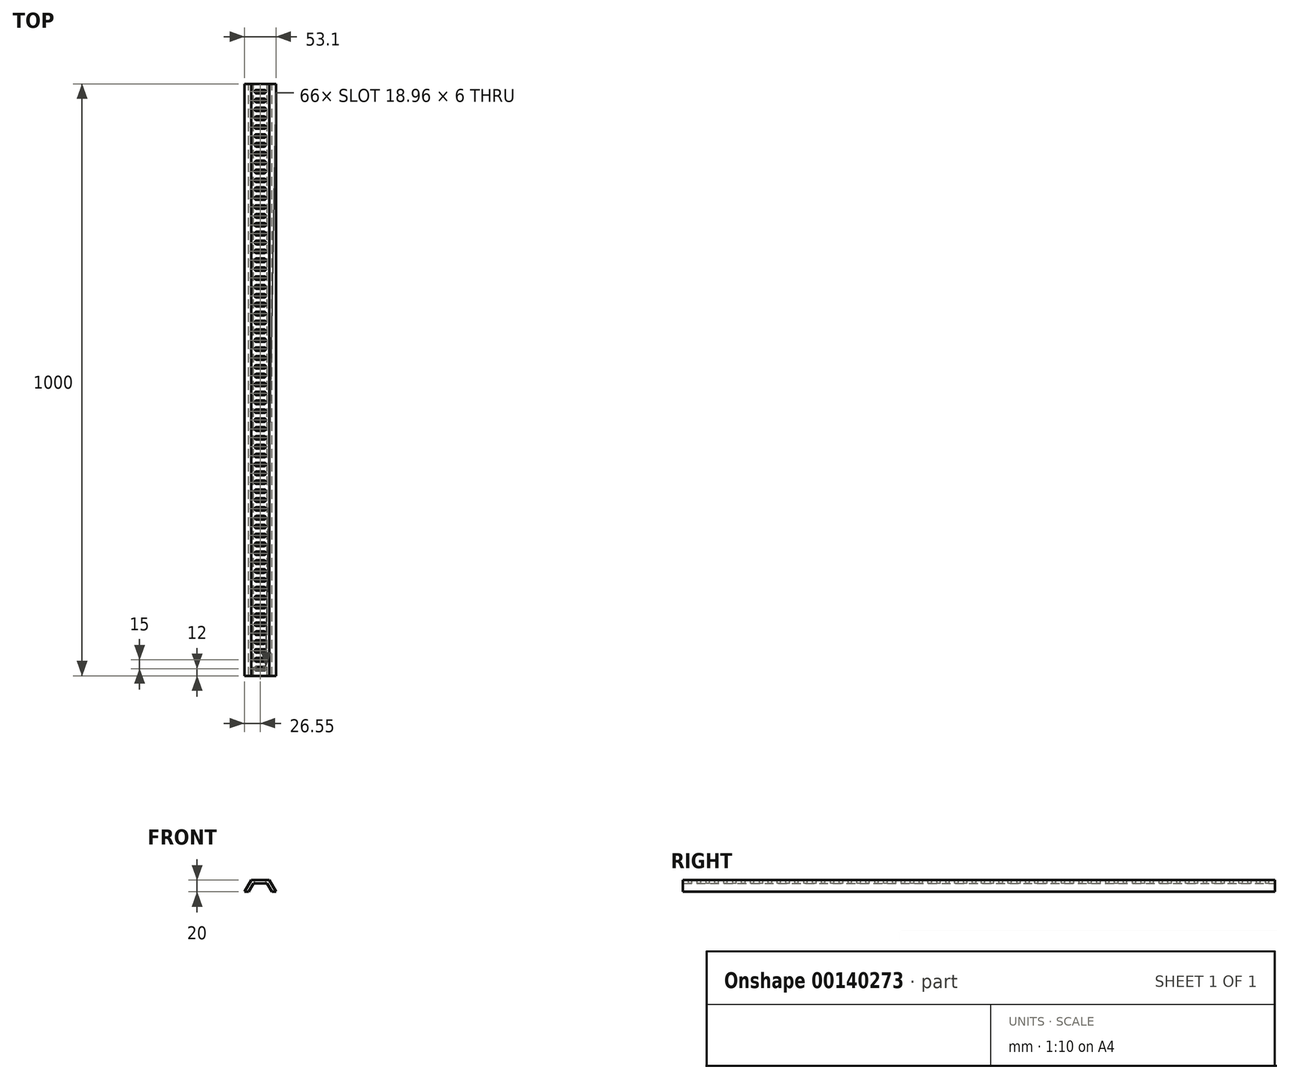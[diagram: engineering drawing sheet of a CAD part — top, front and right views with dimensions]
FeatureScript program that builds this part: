
annotation { "Feature Type Name" : "Feature", "Feature Type Description" : "" }
export const myFeature = defineFeature(function(context is Context, id is Id, definition is map)
    precondition{}
    {
        {
            var Q0;
            Q0=qCreatedBy(makeId("Front.planeOp"),FACE);
            var sketch = newSketch(context, id + "F0", { "sketchPlane" : qUnion([Q0])});
            skLineSegment(sketch, "E0", {"start": v(0, 20) * mm, "end": v(-49.9, 20) * mm, "construction": true});
            skLineSegment(sketch, "E1", {"start": v(0, 14) * mm, "end": v(-49.9, 14) * mm, "construction": true});
            skLineSegment(sketch, "E2", {"start": v(0, 20) * mm, "end": v(-15, 20) * mm});
            skLineSegment(sketch, "E3", {"start": v(-15, 20) * mm, "end": v(-26.55, 0) * mm});
            skLineSegment(sketch, "E4", {"start": v(-26.55, 0) * mm, "end": v(-19.5, 0) * mm});
            skLineSegment(sketch, "E5", {"start": v(-19.5, 0) * mm, "end": v(-11.41, 14) * mm});
            skLineSegment(sketch, "E6", {"start": v(-11.41, 14) * mm, "end": v(0, 14) * mm});
            skLineSegment(sketch, "E7.MirrorCS", {"start": v(0, 20) * mm, "end": v(15, 20) * mm});
            skLineSegment(sketch, "E8.MirrorCS", {"start": v(11.41, 14) * mm, "end": v(0, 14) * mm});
            skLineSegment(sketch, "E9.MirrorCS", {"start": v(19.5, 0) * mm, "end": v(11.41, 14) * mm});
            skLineSegment(sketch, "E10.MirrorCS", {"start": v(26.55, 0) * mm, "end": v(19.5, 0) * mm});
            skLineSegment(sketch, "E11.MirrorCS", {"start": v(15, 20) * mm, "end": v(26.55, 0) * mm});
            skLineSegment(sketch, "E12", {"start": v(-19.5, 0) * mm, "end": v(-24.78, 3.05) * mm, "construction": true});
            skSolve(sketch);
        }
        {
            var Q0;
            Q0=makeQuery(id+"F0.imprint","IMPRINT",FACE,{"disambiguationData":[TD([[makeQuery(id+"F0.imprint","IMPRINT",EDGE,{"derivedFrom":sQuery(id+"F0.wireOp",EDGE,"E2")}),1.0]])]});
            extrude(context, id + "F1", {"entities" : qUnion([Q0]), "depth" : 1000 * mm});
        }
        {
            var Q0;
            Q0=makeQuery(id+"F1.opExtrude","SWEPT_FACE",FACE,{"disambiguationData":[OSD([sQuery(id+"F0.wireOp",EDGE,"E2"),sQuery(id+"F0.wireOp",EDGE,"E7.MirrorCS")])]});
            var sketch = newSketch(context, id + "F2", { "sketchPlane" : qUnion([Q0])});
            skLineSegment(sketch, "E13.bottom", {"start": v(-6.48, -985) * mm, "end": v(6.48, -985) * mm});
            skLineSegment(sketch, "E13.top", {"start": v(-6.48, -991) * mm, "end": v(6.48, -991) * mm});
            skLineSegment(sketch, "E13.left", {"start": v(-9.48, -988) * mm, "end": v(-9.48, -988) * mm});
            skLineSegment(sketch, "E13.right", {"start": v(9.48, -988) * mm, "end": v(9.48, -988) * mm});
            skPoint(sketch, "E13.middle", {"position": v(0, -988) * mm});
            skPoint(sketch, "E14.visualSharp", {"position": v(-9.48, -985) * mm});
            skArc(sketch, "E14.filletArc", {"start": v(-6.48, -985) * mm, "mid": v(-8.6, -985.88) * mm, "end": v(-9.48, -988) * mm});
            skPoint(sketch, "E15.visualSharp", {"position": v(-9.48, -991) * mm});
            skArc(sketch, "E15.filletArc", {"start": v(-9.48, -988) * mm, "mid": v(-8.6, -990.12) * mm, "end": v(-6.48, -991) * mm});
            skPoint(sketch, "E16.visualSharp", {"position": v(9.48, -985) * mm});
            skArc(sketch, "E16.filletArc", {"start": v(9.48, -988) * mm, "mid": v(8.6, -985.88) * mm, "end": v(6.48, -985) * mm});
            skPoint(sketch, "E17.visualSharp", {"position": v(9.48, -991) * mm});
            skArc(sketch, "E17.filletArc", {"start": v(6.48, -991) * mm, "mid": v(8.6, -990.12) * mm, "end": v(9.48, -988) * mm});
            skLineSegment(sketch, "E18.0.1.0", {"start": v(-6.48, -976) * mm, "end": v(6.48, -976) * mm});
            skLineSegment(sketch, "E18.0.1.1", {"start": v(-6.48, -970) * mm, "end": v(6.48, -970) * mm});
            skPoint(sketch, "E18.0.1.2", {"position": v(9.48, -970) * mm});
            skPoint(sketch, "E18.0.1.3", {"position": v(-9.48, -976) * mm});
            skPoint(sketch, "E18.0.1.4", {"position": v(9.48, -976) * mm});
            skPoint(sketch, "E18.0.1.5", {"position": v(-9.48, -970) * mm});
            skPoint(sketch, "E18.0.1.6", {"position": v(0, -973) * mm});
            skArc(sketch, "E18.0.1.7", {"start": v(-9.48, -973) * mm, "mid": v(-8.6, -975.12) * mm, "end": v(-6.48, -976) * mm});
            skArc(sketch, "E18.0.1.8", {"start": v(-6.48, -970) * mm, "mid": v(-8.6, -970.88) * mm, "end": v(-9.48, -973) * mm});
            skArc(sketch, "E18.0.1.9", {"start": v(9.48, -973) * mm, "mid": v(8.6, -970.88) * mm, "end": v(6.48, -970) * mm});
            skArc(sketch, "E18.0.1.10", {"start": v(6.48, -976) * mm, "mid": v(8.6, -975.12) * mm, "end": v(9.48, -973) * mm});
            skLineSegment(sketch, "E18.0.2.0", {"start": v(-6.48, -961) * mm, "end": v(6.48, -961) * mm});
            skLineSegment(sketch, "E18.0.2.1", {"start": v(-6.48, -955) * mm, "end": v(6.48, -955) * mm});
            skPoint(sketch, "E18.0.2.2", {"position": v(9.48, -955) * mm});
            skPoint(sketch, "E18.0.2.3", {"position": v(-9.48, -961) * mm});
            skPoint(sketch, "E18.0.2.4", {"position": v(9.48, -961) * mm});
            skPoint(sketch, "E18.0.2.5", {"position": v(-9.48, -955) * mm});
            skPoint(sketch, "E18.0.2.6", {"position": v(0, -958) * mm});
            skArc(sketch, "E18.0.2.7", {"start": v(-9.48, -958) * mm, "mid": v(-8.6, -960.12) * mm, "end": v(-6.48, -961) * mm});
            skArc(sketch, "E18.0.2.8", {"start": v(-6.48, -955) * mm, "mid": v(-8.6, -955.88) * mm, "end": v(-9.48, -958) * mm});
            skArc(sketch, "E18.0.2.9", {"start": v(9.48, -958) * mm, "mid": v(8.6, -955.88) * mm, "end": v(6.48, -955) * mm});
            skArc(sketch, "E18.0.2.10", {"start": v(6.48, -961) * mm, "mid": v(8.6, -960.12) * mm, "end": v(9.48, -958) * mm});
            skLineSegment(sketch, "E18.0.3.0", {"start": v(-6.48, -946) * mm, "end": v(6.48, -946) * mm});
            skLineSegment(sketch, "E18.0.3.1", {"start": v(-6.48, -940) * mm, "end": v(6.48, -940) * mm});
            skPoint(sketch, "E18.0.3.2", {"position": v(9.48, -940) * mm});
            skPoint(sketch, "E18.0.3.3", {"position": v(-9.48, -946) * mm});
            skPoint(sketch, "E18.0.3.4", {"position": v(9.48, -946) * mm});
            skPoint(sketch, "E18.0.3.5", {"position": v(-9.48, -940) * mm});
            skPoint(sketch, "E18.0.3.6", {"position": v(0, -943) * mm});
            skArc(sketch, "E18.0.3.7", {"start": v(-9.48, -943) * mm, "mid": v(-8.6, -945.12) * mm, "end": v(-6.48, -946) * mm});
            skArc(sketch, "E18.0.3.8", {"start": v(-6.48, -940) * mm, "mid": v(-8.6, -940.88) * mm, "end": v(-9.48, -943) * mm});
            skArc(sketch, "E18.0.3.9", {"start": v(9.48, -943) * mm, "mid": v(8.6, -940.88) * mm, "end": v(6.48, -940) * mm});
            skArc(sketch, "E18.0.3.10", {"start": v(6.48, -946) * mm, "mid": v(8.6, -945.12) * mm, "end": v(9.48, -943) * mm});
            skLineSegment(sketch, "E18.0.4.0", {"start": v(-6.48, -931) * mm, "end": v(6.48, -931) * mm});
            skLineSegment(sketch, "E18.0.4.1", {"start": v(-6.48, -925) * mm, "end": v(6.48, -925) * mm});
            skPoint(sketch, "E18.0.4.2", {"position": v(9.48, -925) * mm});
            skPoint(sketch, "E18.0.4.3", {"position": v(-9.48, -931) * mm});
            skPoint(sketch, "E18.0.4.4", {"position": v(9.48, -931) * mm});
            skPoint(sketch, "E18.0.4.5", {"position": v(-9.48, -925) * mm});
            skPoint(sketch, "E18.0.4.6", {"position": v(0, -928) * mm});
            skArc(sketch, "E18.0.4.7", {"start": v(-9.48, -928) * mm, "mid": v(-8.6, -930.12) * mm, "end": v(-6.48, -931) * mm});
            skArc(sketch, "E18.0.4.8", {"start": v(-6.48, -925) * mm, "mid": v(-8.6, -925.88) * mm, "end": v(-9.48, -928) * mm});
            skArc(sketch, "E18.0.4.9", {"start": v(9.48, -928) * mm, "mid": v(8.6, -925.88) * mm, "end": v(6.48, -925) * mm});
            skArc(sketch, "E18.0.4.10", {"start": v(6.48, -931) * mm, "mid": v(8.6, -930.12) * mm, "end": v(9.48, -928) * mm});
            skLineSegment(sketch, "E18.0.5.0", {"start": v(-6.48, -916) * mm, "end": v(6.48, -916) * mm});
            skLineSegment(sketch, "E18.0.5.1", {"start": v(-6.48, -910) * mm, "end": v(6.48, -910) * mm});
            skPoint(sketch, "E18.0.5.2", {"position": v(9.48, -910) * mm});
            skPoint(sketch, "E18.0.5.3", {"position": v(-9.48, -916) * mm});
            skPoint(sketch, "E18.0.5.4", {"position": v(9.48, -916) * mm});
            skPoint(sketch, "E18.0.5.5", {"position": v(-9.48, -910) * mm});
            skPoint(sketch, "E18.0.5.6", {"position": v(0, -913) * mm});
            skArc(sketch, "E18.0.5.7", {"start": v(-9.48, -913) * mm, "mid": v(-8.6, -915.12) * mm, "end": v(-6.48, -916) * mm});
            skArc(sketch, "E18.0.5.8", {"start": v(-6.48, -910) * mm, "mid": v(-8.6, -910.88) * mm, "end": v(-9.48, -913) * mm});
            skArc(sketch, "E18.0.5.9", {"start": v(9.48, -913) * mm, "mid": v(8.6, -910.88) * mm, "end": v(6.48, -910) * mm});
            skArc(sketch, "E18.0.5.10", {"start": v(6.48, -916) * mm, "mid": v(8.6, -915.12) * mm, "end": v(9.48, -913) * mm});
            skLineSegment(sketch, "E18.0.6.0", {"start": v(-6.48, -901) * mm, "end": v(6.48, -901) * mm});
            skLineSegment(sketch, "E18.0.6.1", {"start": v(-6.48, -895) * mm, "end": v(6.48, -895) * mm});
            skPoint(sketch, "E18.0.6.2", {"position": v(9.48, -895) * mm});
            skPoint(sketch, "E18.0.6.3", {"position": v(-9.48, -901) * mm});
            skPoint(sketch, "E18.0.6.4", {"position": v(9.48, -901) * mm});
            skPoint(sketch, "E18.0.6.5", {"position": v(-9.48, -895) * mm});
            skPoint(sketch, "E18.0.6.6", {"position": v(0, -898) * mm});
            skArc(sketch, "E18.0.6.7", {"start": v(-9.48, -898) * mm, "mid": v(-8.6, -900.12) * mm, "end": v(-6.48, -901) * mm});
            skArc(sketch, "E18.0.6.8", {"start": v(-6.48, -895) * mm, "mid": v(-8.6, -895.88) * mm, "end": v(-9.48, -898) * mm});
            skArc(sketch, "E18.0.6.9", {"start": v(9.48, -898) * mm, "mid": v(8.6, -895.88) * mm, "end": v(6.48, -895) * mm});
            skArc(sketch, "E18.0.6.10", {"start": v(6.48, -901) * mm, "mid": v(8.6, -900.12) * mm, "end": v(9.48, -898) * mm});
            skLineSegment(sketch, "E18.0.7.0", {"start": v(-6.48, -886) * mm, "end": v(6.48, -886) * mm});
            skLineSegment(sketch, "E18.0.7.1", {"start": v(-6.48, -880) * mm, "end": v(6.48, -880) * mm});
            skPoint(sketch, "E18.0.7.2", {"position": v(9.48, -880) * mm});
            skPoint(sketch, "E18.0.7.3", {"position": v(-9.48, -886) * mm});
            skPoint(sketch, "E18.0.7.4", {"position": v(9.48, -886) * mm});
            skPoint(sketch, "E18.0.7.5", {"position": v(-9.48, -880) * mm});
            skPoint(sketch, "E18.0.7.6", {"position": v(0, -883) * mm});
            skArc(sketch, "E18.0.7.7", {"start": v(-9.48, -883) * mm, "mid": v(-8.6, -885.12) * mm, "end": v(-6.48, -886) * mm});
            skArc(sketch, "E18.0.7.8", {"start": v(-6.48, -880) * mm, "mid": v(-8.6, -880.88) * mm, "end": v(-9.48, -883) * mm});
            skArc(sketch, "E18.0.7.9", {"start": v(9.48, -883) * mm, "mid": v(8.6, -880.88) * mm, "end": v(6.48, -880) * mm});
            skArc(sketch, "E18.0.7.10", {"start": v(6.48, -886) * mm, "mid": v(8.6, -885.12) * mm, "end": v(9.48, -883) * mm});
            skLineSegment(sketch, "E18.0.8.0", {"start": v(-6.48, -871) * mm, "end": v(6.48, -871) * mm});
            skLineSegment(sketch, "E18.0.8.1", {"start": v(-6.48, -865) * mm, "end": v(6.48, -865) * mm});
            skPoint(sketch, "E18.0.8.2", {"position": v(9.48, -865) * mm});
            skPoint(sketch, "E18.0.8.3", {"position": v(-9.48, -871) * mm});
            skPoint(sketch, "E18.0.8.4", {"position": v(9.48, -871) * mm});
            skPoint(sketch, "E18.0.8.5", {"position": v(-9.48, -865) * mm});
            skPoint(sketch, "E18.0.8.6", {"position": v(0, -868) * mm});
            skArc(sketch, "E18.0.8.7", {"start": v(-9.48, -868) * mm, "mid": v(-8.6, -870.12) * mm, "end": v(-6.48, -871) * mm});
            skArc(sketch, "E18.0.8.8", {"start": v(-6.48, -865) * mm, "mid": v(-8.6, -865.88) * mm, "end": v(-9.48, -868) * mm});
            skArc(sketch, "E18.0.8.9", {"start": v(9.48, -868) * mm, "mid": v(8.6, -865.88) * mm, "end": v(6.48, -865) * mm});
            skArc(sketch, "E18.0.8.10", {"start": v(6.48, -871) * mm, "mid": v(8.6, -870.12) * mm, "end": v(9.48, -868) * mm});
            skLineSegment(sketch, "E18.0.9.0", {"start": v(-6.48, -856) * mm, "end": v(6.48, -856) * mm});
            skLineSegment(sketch, "E18.0.9.1", {"start": v(-6.48, -850) * mm, "end": v(6.48, -850) * mm});
            skPoint(sketch, "E18.0.9.2", {"position": v(9.48, -850) * mm});
            skPoint(sketch, "E18.0.9.3", {"position": v(-9.48, -856) * mm});
            skPoint(sketch, "E18.0.9.4", {"position": v(9.48, -856) * mm});
            skPoint(sketch, "E18.0.9.5", {"position": v(-9.48, -850) * mm});
            skPoint(sketch, "E18.0.9.6", {"position": v(0, -853) * mm});
            skArc(sketch, "E18.0.9.7", {"start": v(-9.48, -853) * mm, "mid": v(-8.6, -855.12) * mm, "end": v(-6.48, -856) * mm});
            skArc(sketch, "E18.0.9.8", {"start": v(-6.48, -850) * mm, "mid": v(-8.6, -850.88) * mm, "end": v(-9.48, -853) * mm});
            skArc(sketch, "E18.0.9.9", {"start": v(9.48, -853) * mm, "mid": v(8.6, -850.88) * mm, "end": v(6.48, -850) * mm});
            skArc(sketch, "E18.0.9.10", {"start": v(6.48, -856) * mm, "mid": v(8.6, -855.12) * mm, "end": v(9.48, -853) * mm});
            skLineSegment(sketch, "E18.0.10.0", {"start": v(-6.48, -841) * mm, "end": v(6.48, -841) * mm});
            skLineSegment(sketch, "E18.0.10.1", {"start": v(-6.48, -835) * mm, "end": v(6.48, -835) * mm});
            skPoint(sketch, "E18.0.10.2", {"position": v(9.48, -835) * mm});
            skPoint(sketch, "E18.0.10.3", {"position": v(-9.48, -841) * mm});
            skPoint(sketch, "E18.0.10.4", {"position": v(9.48, -841) * mm});
            skPoint(sketch, "E18.0.10.5", {"position": v(-9.48, -835) * mm});
            skPoint(sketch, "E18.0.10.6", {"position": v(0, -838) * mm});
            skArc(sketch, "E18.0.10.7", {"start": v(-9.48, -838) * mm, "mid": v(-8.6, -840.12) * mm, "end": v(-6.48, -841) * mm});
            skArc(sketch, "E18.0.10.8", {"start": v(-6.48, -835) * mm, "mid": v(-8.6, -835.88) * mm, "end": v(-9.48, -838) * mm});
            skArc(sketch, "E18.0.10.9", {"start": v(9.48, -838) * mm, "mid": v(8.6, -835.88) * mm, "end": v(6.48, -835) * mm});
            skArc(sketch, "E18.0.10.10", {"start": v(6.48, -841) * mm, "mid": v(8.6, -840.12) * mm, "end": v(9.48, -838) * mm});
            skLineSegment(sketch, "E18.0.11.0", {"start": v(-6.48, -826) * mm, "end": v(6.48, -826) * mm});
            skLineSegment(sketch, "E18.0.11.1", {"start": v(-6.48, -820) * mm, "end": v(6.48, -820) * mm});
            skPoint(sketch, "E18.0.11.2", {"position": v(9.48, -820) * mm});
            skPoint(sketch, "E18.0.11.3", {"position": v(-9.48, -826) * mm});
            skPoint(sketch, "E18.0.11.4", {"position": v(9.48, -826) * mm});
            skPoint(sketch, "E18.0.11.5", {"position": v(-9.48, -820) * mm});
            skPoint(sketch, "E18.0.11.6", {"position": v(0, -823) * mm});
            skArc(sketch, "E18.0.11.7", {"start": v(-9.48, -823) * mm, "mid": v(-8.6, -825.12) * mm, "end": v(-6.48, -826) * mm});
            skArc(sketch, "E18.0.11.8", {"start": v(-6.48, -820) * mm, "mid": v(-8.6, -820.88) * mm, "end": v(-9.48, -823) * mm});
            skArc(sketch, "E18.0.11.9", {"start": v(9.48, -823) * mm, "mid": v(8.6, -820.88) * mm, "end": v(6.48, -820) * mm});
            skArc(sketch, "E18.0.11.10", {"start": v(6.48, -826) * mm, "mid": v(8.6, -825.12) * mm, "end": v(9.48, -823) * mm});
            skLineSegment(sketch, "E18.0.12.0", {"start": v(-6.48, -811) * mm, "end": v(6.48, -811) * mm});
            skLineSegment(sketch, "E18.0.12.1", {"start": v(-6.48, -805) * mm, "end": v(6.48, -805) * mm});
            skPoint(sketch, "E18.0.12.2", {"position": v(9.48, -805) * mm});
            skPoint(sketch, "E18.0.12.3", {"position": v(-9.48, -811) * mm});
            skPoint(sketch, "E18.0.12.4", {"position": v(9.48, -811) * mm});
            skPoint(sketch, "E18.0.12.5", {"position": v(-9.48, -805) * mm});
            skPoint(sketch, "E18.0.12.6", {"position": v(0, -808) * mm});
            skArc(sketch, "E18.0.12.7", {"start": v(-9.48, -808) * mm, "mid": v(-8.6, -810.12) * mm, "end": v(-6.48, -811) * mm});
            skArc(sketch, "E18.0.12.8", {"start": v(-6.48, -805) * mm, "mid": v(-8.6, -805.88) * mm, "end": v(-9.48, -808) * mm});
            skArc(sketch, "E18.0.12.9", {"start": v(9.48, -808) * mm, "mid": v(8.6, -805.88) * mm, "end": v(6.48, -805) * mm});
            skArc(sketch, "E18.0.12.10", {"start": v(6.48, -811) * mm, "mid": v(8.6, -810.12) * mm, "end": v(9.48, -808) * mm});
            skLineSegment(sketch, "E18.0.13.0", {"start": v(-6.48, -796) * mm, "end": v(6.48, -796) * mm});
            skLineSegment(sketch, "E18.0.13.1", {"start": v(-6.48, -790) * mm, "end": v(6.48, -790) * mm});
            skPoint(sketch, "E18.0.13.2", {"position": v(9.48, -790) * mm});
            skPoint(sketch, "E18.0.13.3", {"position": v(-9.48, -796) * mm});
            skPoint(sketch, "E18.0.13.4", {"position": v(9.48, -796) * mm});
            skPoint(sketch, "E18.0.13.5", {"position": v(-9.48, -790) * mm});
            skPoint(sketch, "E18.0.13.6", {"position": v(0, -793) * mm});
            skArc(sketch, "E18.0.13.7", {"start": v(-9.48, -793) * mm, "mid": v(-8.6, -795.12) * mm, "end": v(-6.48, -796) * mm});
            skArc(sketch, "E18.0.13.8", {"start": v(-6.48, -790) * mm, "mid": v(-8.6, -790.88) * mm, "end": v(-9.48, -793) * mm});
            skArc(sketch, "E18.0.13.9", {"start": v(9.48, -793) * mm, "mid": v(8.6, -790.88) * mm, "end": v(6.48, -790) * mm});
            skArc(sketch, "E18.0.13.10", {"start": v(6.48, -796) * mm, "mid": v(8.6, -795.12) * mm, "end": v(9.48, -793) * mm});
            skLineSegment(sketch, "E18.0.14.0", {"start": v(-6.48, -781) * mm, "end": v(6.48, -781) * mm});
            skLineSegment(sketch, "E18.0.14.1", {"start": v(-6.48, -775) * mm, "end": v(6.48, -775) * mm});
            skPoint(sketch, "E18.0.14.2", {"position": v(9.48, -775) * mm});
            skPoint(sketch, "E18.0.14.3", {"position": v(-9.48, -781) * mm});
            skPoint(sketch, "E18.0.14.4", {"position": v(9.48, -781) * mm});
            skPoint(sketch, "E18.0.14.5", {"position": v(-9.48, -775) * mm});
            skPoint(sketch, "E18.0.14.6", {"position": v(0, -778) * mm});
            skArc(sketch, "E18.0.14.7", {"start": v(-9.48, -778) * mm, "mid": v(-8.6, -780.12) * mm, "end": v(-6.48, -781) * mm});
            skArc(sketch, "E18.0.14.8", {"start": v(-6.48, -775) * mm, "mid": v(-8.6, -775.88) * mm, "end": v(-9.48, -778) * mm});
            skArc(sketch, "E18.0.14.9", {"start": v(9.48, -778) * mm, "mid": v(8.6, -775.88) * mm, "end": v(6.48, -775) * mm});
            skArc(sketch, "E18.0.14.10", {"start": v(6.48, -781) * mm, "mid": v(8.6, -780.12) * mm, "end": v(9.48, -778) * mm});
            skLineSegment(sketch, "E18.direction1", {"start": v(-9.48, -991) * mm, "end": v(21.55, -991) * mm, "construction": true});
            skLineSegment(sketch, "E18.direction2", {"start": v(-9.48, -991) * mm, "end": v(-9.48, -976) * mm, "construction": true});
            skLineSegment(sketch, "E19.0.0.15", {"start": v(-6.48, -766) * mm, "end": v(6.48, -766) * mm});
            skLineSegment(sketch, "E19.3.0.15", {"start": v(-6.48, -760) * mm, "end": v(6.48, -760) * mm});
            skPoint(sketch, "E19.6.0.15", {"position": v(9.48, -760) * mm});
            skPoint(sketch, "E19.7.0.15", {"position": v(-9.48, -766) * mm});
            skPoint(sketch, "E19.8.0.15", {"position": v(9.48, -766) * mm});
            skPoint(sketch, "E19.9.0.15", {"position": v(-9.48, -760) * mm});
            skPoint(sketch, "E19.10.0.15", {"position": v(0, -763) * mm});
            skArc(sketch, "E19.11.0.15", {"start": v(-9.48, -763) * mm, "mid": v(-8.6, -765.12) * mm, "end": v(-6.48, -766) * mm});
            skArc(sketch, "E19.15.0.15", {"start": v(-6.48, -760) * mm, "mid": v(-8.6, -760.88) * mm, "end": v(-9.48, -763) * mm});
            skArc(sketch, "E19.19.0.15", {"start": v(9.48, -763) * mm, "mid": v(8.6, -760.88) * mm, "end": v(6.48, -760) * mm});
            skArc(sketch, "E19.23.0.15", {"start": v(6.48, -766) * mm, "mid": v(8.6, -765.12) * mm, "end": v(9.48, -763) * mm});
            skLineSegment(sketch, "E19.0.0.16", {"start": v(-6.48, -751) * mm, "end": v(6.48, -751) * mm});
            skLineSegment(sketch, "E19.3.0.16", {"start": v(-6.48, -745) * mm, "end": v(6.48, -745) * mm});
            skPoint(sketch, "E19.6.0.16", {"position": v(9.48, -745) * mm});
            skPoint(sketch, "E19.7.0.16", {"position": v(-9.48, -751) * mm});
            skPoint(sketch, "E19.8.0.16", {"position": v(9.48, -751) * mm});
            skPoint(sketch, "E19.9.0.16", {"position": v(-9.48, -745) * mm});
            skPoint(sketch, "E19.10.0.16", {"position": v(0, -748) * mm});
            skArc(sketch, "E19.11.0.16", {"start": v(-9.48, -748) * mm, "mid": v(-8.6, -750.12) * mm, "end": v(-6.48, -751) * mm});
            skArc(sketch, "E19.15.0.16", {"start": v(-6.48, -745) * mm, "mid": v(-8.6, -745.88) * mm, "end": v(-9.48, -748) * mm});
            skArc(sketch, "E19.19.0.16", {"start": v(9.48, -748) * mm, "mid": v(8.6, -745.88) * mm, "end": v(6.48, -745) * mm});
            skArc(sketch, "E19.23.0.16", {"start": v(6.48, -751) * mm, "mid": v(8.6, -750.12) * mm, "end": v(9.48, -748) * mm});
            skLineSegment(sketch, "E19.0.0.17", {"start": v(-6.48, -736) * mm, "end": v(6.48, -736) * mm});
            skLineSegment(sketch, "E19.3.0.17", {"start": v(-6.48, -730) * mm, "end": v(6.48, -730) * mm});
            skPoint(sketch, "E19.6.0.17", {"position": v(9.48, -730) * mm});
            skPoint(sketch, "E19.7.0.17", {"position": v(-9.48, -736) * mm});
            skPoint(sketch, "E19.8.0.17", {"position": v(9.48, -736) * mm});
            skPoint(sketch, "E19.9.0.17", {"position": v(-9.48, -730) * mm});
            skPoint(sketch, "E19.10.0.17", {"position": v(0, -733) * mm});
            skArc(sketch, "E19.11.0.17", {"start": v(-9.48, -733) * mm, "mid": v(-8.6, -735.12) * mm, "end": v(-6.48, -736) * mm});
            skArc(sketch, "E19.15.0.17", {"start": v(-6.48, -730) * mm, "mid": v(-8.6, -730.88) * mm, "end": v(-9.48, -733) * mm});
            skArc(sketch, "E19.19.0.17", {"start": v(9.48, -733) * mm, "mid": v(8.6, -730.88) * mm, "end": v(6.48, -730) * mm});
            skArc(sketch, "E19.23.0.17", {"start": v(6.48, -736) * mm, "mid": v(8.6, -735.12) * mm, "end": v(9.48, -733) * mm});
            skLineSegment(sketch, "E19.0.0.18", {"start": v(-6.48, -721) * mm, "end": v(6.48, -721) * mm});
            skLineSegment(sketch, "E19.3.0.18", {"start": v(-6.48, -715) * mm, "end": v(6.48, -715) * mm});
            skPoint(sketch, "E19.6.0.18", {"position": v(9.48, -715) * mm});
            skPoint(sketch, "E19.7.0.18", {"position": v(-9.48, -721) * mm});
            skPoint(sketch, "E19.8.0.18", {"position": v(9.48, -721) * mm});
            skPoint(sketch, "E19.9.0.18", {"position": v(-9.48, -715) * mm});
            skPoint(sketch, "E19.10.0.18", {"position": v(0, -718) * mm});
            skArc(sketch, "E19.11.0.18", {"start": v(-9.48, -718) * mm, "mid": v(-8.6, -720.12) * mm, "end": v(-6.48, -721) * mm});
            skArc(sketch, "E19.15.0.18", {"start": v(-6.48, -715) * mm, "mid": v(-8.6, -715.88) * mm, "end": v(-9.48, -718) * mm});
            skArc(sketch, "E19.19.0.18", {"start": v(9.48, -718) * mm, "mid": v(8.6, -715.88) * mm, "end": v(6.48, -715) * mm});
            skArc(sketch, "E19.23.0.18", {"start": v(6.48, -721) * mm, "mid": v(8.6, -720.12) * mm, "end": v(9.48, -718) * mm});
            skLineSegment(sketch, "E19.0.0.19", {"start": v(-6.48, -706) * mm, "end": v(6.48, -706) * mm});
            skLineSegment(sketch, "E19.3.0.19", {"start": v(-6.48, -700) * mm, "end": v(6.48, -700) * mm});
            skPoint(sketch, "E19.6.0.19", {"position": v(9.48, -700) * mm});
            skPoint(sketch, "E19.7.0.19", {"position": v(-9.48, -706) * mm});
            skPoint(sketch, "E19.8.0.19", {"position": v(9.48, -706) * mm});
            skPoint(sketch, "E19.9.0.19", {"position": v(-9.48, -700) * mm});
            skPoint(sketch, "E19.10.0.19", {"position": v(0, -703) * mm});
            skArc(sketch, "E19.11.0.19", {"start": v(-9.48, -703) * mm, "mid": v(-8.6, -705.12) * mm, "end": v(-6.48, -706) * mm});
            skArc(sketch, "E19.15.0.19", {"start": v(-6.48, -700) * mm, "mid": v(-8.6, -700.88) * mm, "end": v(-9.48, -703) * mm});
            skArc(sketch, "E19.19.0.19", {"start": v(9.48, -703) * mm, "mid": v(8.6, -700.88) * mm, "end": v(6.48, -700) * mm});
            skArc(sketch, "E19.23.0.19", {"start": v(6.48, -706) * mm, "mid": v(8.6, -705.12) * mm, "end": v(9.48, -703) * mm});
            skLineSegment(sketch, "E19.0.0.20", {"start": v(-6.48, -691) * mm, "end": v(6.48, -691) * mm});
            skLineSegment(sketch, "E19.3.0.20", {"start": v(-6.48, -685) * mm, "end": v(6.48, -685) * mm});
            skPoint(sketch, "E19.6.0.20", {"position": v(9.48, -685) * mm});
            skPoint(sketch, "E19.7.0.20", {"position": v(-9.48, -691) * mm});
            skPoint(sketch, "E19.8.0.20", {"position": v(9.48, -691) * mm});
            skPoint(sketch, "E19.9.0.20", {"position": v(-9.48, -685) * mm});
            skPoint(sketch, "E19.10.0.20", {"position": v(0, -688) * mm});
            skArc(sketch, "E19.11.0.20", {"start": v(-9.48, -688) * mm, "mid": v(-8.6, -690.12) * mm, "end": v(-6.48, -691) * mm});
            skArc(sketch, "E19.15.0.20", {"start": v(-6.48, -685) * mm, "mid": v(-8.6, -685.88) * mm, "end": v(-9.48, -688) * mm});
            skArc(sketch, "E19.19.0.20", {"start": v(9.48, -688) * mm, "mid": v(8.6, -685.88) * mm, "end": v(6.48, -685) * mm});
            skArc(sketch, "E19.23.0.20", {"start": v(6.48, -691) * mm, "mid": v(8.6, -690.12) * mm, "end": v(9.48, -688) * mm});
            skLineSegment(sketch, "E19.0.0.21", {"start": v(-6.48, -676) * mm, "end": v(6.48, -676) * mm});
            skLineSegment(sketch, "E19.3.0.21", {"start": v(-6.48, -670) * mm, "end": v(6.48, -670) * mm});
            skPoint(sketch, "E19.6.0.21", {"position": v(9.48, -670) * mm});
            skPoint(sketch, "E19.7.0.21", {"position": v(-9.48, -676) * mm});
            skPoint(sketch, "E19.8.0.21", {"position": v(9.48, -676) * mm});
            skPoint(sketch, "E19.9.0.21", {"position": v(-9.48, -670) * mm});
            skPoint(sketch, "E19.10.0.21", {"position": v(0, -673) * mm});
            skArc(sketch, "E19.11.0.21", {"start": v(-9.48, -673) * mm, "mid": v(-8.6, -675.12) * mm, "end": v(-6.48, -676) * mm});
            skArc(sketch, "E19.15.0.21", {"start": v(-6.48, -670) * mm, "mid": v(-8.6, -670.88) * mm, "end": v(-9.48, -673) * mm});
            skArc(sketch, "E19.19.0.21", {"start": v(9.48, -673) * mm, "mid": v(8.6, -670.88) * mm, "end": v(6.48, -670) * mm});
            skArc(sketch, "E19.23.0.21", {"start": v(6.48, -676) * mm, "mid": v(8.6, -675.12) * mm, "end": v(9.48, -673) * mm});
            skLineSegment(sketch, "E19.0.0.22", {"start": v(-6.48, -661) * mm, "end": v(6.48, -661) * mm});
            skLineSegment(sketch, "E19.3.0.22", {"start": v(-6.48, -655) * mm, "end": v(6.48, -655) * mm});
            skPoint(sketch, "E19.6.0.22", {"position": v(9.48, -655) * mm});
            skPoint(sketch, "E19.7.0.22", {"position": v(-9.48, -661) * mm});
            skPoint(sketch, "E19.8.0.22", {"position": v(9.48, -661) * mm});
            skPoint(sketch, "E19.9.0.22", {"position": v(-9.48, -655) * mm});
            skPoint(sketch, "E19.10.0.22", {"position": v(0, -658) * mm});
            skArc(sketch, "E19.11.0.22", {"start": v(-9.48, -658) * mm, "mid": v(-8.6, -660.12) * mm, "end": v(-6.48, -661) * mm});
            skArc(sketch, "E19.15.0.22", {"start": v(-6.48, -655) * mm, "mid": v(-8.6, -655.88) * mm, "end": v(-9.48, -658) * mm});
            skArc(sketch, "E19.19.0.22", {"start": v(9.48, -658) * mm, "mid": v(8.6, -655.88) * mm, "end": v(6.48, -655) * mm});
            skArc(sketch, "E19.23.0.22", {"start": v(6.48, -661) * mm, "mid": v(8.6, -660.12) * mm, "end": v(9.48, -658) * mm});
            skLineSegment(sketch, "E19.0.0.23", {"start": v(-6.48, -646) * mm, "end": v(6.48, -646) * mm});
            skLineSegment(sketch, "E19.3.0.23", {"start": v(-6.48, -640) * mm, "end": v(6.48, -640) * mm});
            skPoint(sketch, "E19.6.0.23", {"position": v(9.48, -640) * mm});
            skPoint(sketch, "E19.7.0.23", {"position": v(-9.48, -646) * mm});
            skPoint(sketch, "E19.8.0.23", {"position": v(9.48, -646) * mm});
            skPoint(sketch, "E19.9.0.23", {"position": v(-9.48, -640) * mm});
            skPoint(sketch, "E19.10.0.23", {"position": v(0, -643) * mm});
            skArc(sketch, "E19.11.0.23", {"start": v(-9.48, -643) * mm, "mid": v(-8.6, -645.12) * mm, "end": v(-6.48, -646) * mm});
            skArc(sketch, "E19.15.0.23", {"start": v(-6.48, -640) * mm, "mid": v(-8.6, -640.88) * mm, "end": v(-9.48, -643) * mm});
            skArc(sketch, "E19.19.0.23", {"start": v(9.48, -643) * mm, "mid": v(8.6, -640.88) * mm, "end": v(6.48, -640) * mm});
            skArc(sketch, "E19.23.0.23", {"start": v(6.48, -646) * mm, "mid": v(8.6, -645.12) * mm, "end": v(9.48, -643) * mm});
            skLineSegment(sketch, "E19.0.0.24", {"start": v(-6.48, -631) * mm, "end": v(6.48, -631) * mm});
            skLineSegment(sketch, "E19.3.0.24", {"start": v(-6.48, -625) * mm, "end": v(6.48, -625) * mm});
            skPoint(sketch, "E19.6.0.24", {"position": v(9.48, -625) * mm});
            skPoint(sketch, "E19.7.0.24", {"position": v(-9.48, -631) * mm});
            skPoint(sketch, "E19.8.0.24", {"position": v(9.48, -631) * mm});
            skPoint(sketch, "E19.9.0.24", {"position": v(-9.48, -625) * mm});
            skPoint(sketch, "E19.10.0.24", {"position": v(0, -628) * mm});
            skArc(sketch, "E19.11.0.24", {"start": v(-9.48, -628) * mm, "mid": v(-8.6, -630.12) * mm, "end": v(-6.48, -631) * mm});
            skArc(sketch, "E19.15.0.24", {"start": v(-6.48, -625) * mm, "mid": v(-8.6, -625.88) * mm, "end": v(-9.48, -628) * mm});
            skArc(sketch, "E19.19.0.24", {"start": v(9.48, -628) * mm, "mid": v(8.6, -625.88) * mm, "end": v(6.48, -625) * mm});
            skArc(sketch, "E19.23.0.24", {"start": v(6.48, -631) * mm, "mid": v(8.6, -630.12) * mm, "end": v(9.48, -628) * mm});
            skLineSegment(sketch, "E19.0.0.25", {"start": v(-6.48, -616) * mm, "end": v(6.48, -616) * mm});
            skLineSegment(sketch, "E19.3.0.25", {"start": v(-6.48, -610) * mm, "end": v(6.48, -610) * mm});
            skPoint(sketch, "E19.6.0.25", {"position": v(9.48, -610) * mm});
            skPoint(sketch, "E19.7.0.25", {"position": v(-9.48, -616) * mm});
            skPoint(sketch, "E19.8.0.25", {"position": v(9.48, -616) * mm});
            skPoint(sketch, "E19.9.0.25", {"position": v(-9.48, -610) * mm});
            skPoint(sketch, "E19.10.0.25", {"position": v(0, -613) * mm});
            skArc(sketch, "E19.11.0.25", {"start": v(-9.48, -613) * mm, "mid": v(-8.6, -615.12) * mm, "end": v(-6.48, -616) * mm});
            skArc(sketch, "E19.15.0.25", {"start": v(-6.48, -610) * mm, "mid": v(-8.6, -610.88) * mm, "end": v(-9.48, -613) * mm});
            skArc(sketch, "E19.19.0.25", {"start": v(9.48, -613) * mm, "mid": v(8.6, -610.88) * mm, "end": v(6.48, -610) * mm});
            skArc(sketch, "E19.23.0.25", {"start": v(6.48, -616) * mm, "mid": v(8.6, -615.12) * mm, "end": v(9.48, -613) * mm});
            skLineSegment(sketch, "E19.0.0.26", {"start": v(-6.48, -601) * mm, "end": v(6.48, -601) * mm});
            skLineSegment(sketch, "E19.3.0.26", {"start": v(-6.48, -595) * mm, "end": v(6.48, -595) * mm});
            skPoint(sketch, "E19.6.0.26", {"position": v(9.48, -595) * mm});
            skPoint(sketch, "E19.7.0.26", {"position": v(-9.48, -601) * mm});
            skPoint(sketch, "E19.8.0.26", {"position": v(9.48, -601) * mm});
            skPoint(sketch, "E19.9.0.26", {"position": v(-9.48, -595) * mm});
            skPoint(sketch, "E19.10.0.26", {"position": v(0, -598) * mm});
            skArc(sketch, "E19.11.0.26", {"start": v(-9.48, -598) * mm, "mid": v(-8.6, -600.12) * mm, "end": v(-6.48, -601) * mm});
            skArc(sketch, "E19.15.0.26", {"start": v(-6.48, -595) * mm, "mid": v(-8.6, -595.88) * mm, "end": v(-9.48, -598) * mm});
            skArc(sketch, "E19.19.0.26", {"start": v(9.48, -598) * mm, "mid": v(8.6, -595.88) * mm, "end": v(6.48, -595) * mm});
            skArc(sketch, "E19.23.0.26", {"start": v(6.48, -601) * mm, "mid": v(8.6, -600.12) * mm, "end": v(9.48, -598) * mm});
            skLineSegment(sketch, "E19.0.0.27", {"start": v(-6.48, -586) * mm, "end": v(6.48, -586) * mm});
            skLineSegment(sketch, "E19.3.0.27", {"start": v(-6.48, -580) * mm, "end": v(6.48, -580) * mm});
            skPoint(sketch, "E19.6.0.27", {"position": v(9.48, -580) * mm});
            skPoint(sketch, "E19.7.0.27", {"position": v(-9.48, -586) * mm});
            skPoint(sketch, "E19.8.0.27", {"position": v(9.48, -586) * mm});
            skPoint(sketch, "E19.9.0.27", {"position": v(-9.48, -580) * mm});
            skPoint(sketch, "E19.10.0.27", {"position": v(0, -583) * mm});
            skArc(sketch, "E19.11.0.27", {"start": v(-9.48, -583) * mm, "mid": v(-8.6, -585.12) * mm, "end": v(-6.48, -586) * mm});
            skArc(sketch, "E19.15.0.27", {"start": v(-6.48, -580) * mm, "mid": v(-8.6, -580.88) * mm, "end": v(-9.48, -583) * mm});
            skArc(sketch, "E19.19.0.27", {"start": v(9.48, -583) * mm, "mid": v(8.6, -580.88) * mm, "end": v(6.48, -580) * mm});
            skArc(sketch, "E19.23.0.27", {"start": v(6.48, -586) * mm, "mid": v(8.6, -585.12) * mm, "end": v(9.48, -583) * mm});
            skLineSegment(sketch, "E19.0.0.28", {"start": v(-6.48, -571) * mm, "end": v(6.48, -571) * mm});
            skLineSegment(sketch, "E19.3.0.28", {"start": v(-6.48, -565) * mm, "end": v(6.48, -565) * mm});
            skPoint(sketch, "E19.6.0.28", {"position": v(9.48, -565) * mm});
            skPoint(sketch, "E19.7.0.28", {"position": v(-9.48, -571) * mm});
            skPoint(sketch, "E19.8.0.28", {"position": v(9.48, -571) * mm});
            skPoint(sketch, "E19.9.0.28", {"position": v(-9.48, -565) * mm});
            skPoint(sketch, "E19.10.0.28", {"position": v(0, -568) * mm});
            skArc(sketch, "E19.11.0.28", {"start": v(-9.48, -568) * mm, "mid": v(-8.6, -570.12) * mm, "end": v(-6.48, -571) * mm});
            skArc(sketch, "E19.15.0.28", {"start": v(-6.48, -565) * mm, "mid": v(-8.6, -565.88) * mm, "end": v(-9.48, -568) * mm});
            skArc(sketch, "E19.19.0.28", {"start": v(9.48, -568) * mm, "mid": v(8.6, -565.88) * mm, "end": v(6.48, -565) * mm});
            skArc(sketch, "E19.23.0.28", {"start": v(6.48, -571) * mm, "mid": v(8.6, -570.12) * mm, "end": v(9.48, -568) * mm});
            skLineSegment(sketch, "E19.0.0.29", {"start": v(-6.48, -556) * mm, "end": v(6.48, -556) * mm});
            skLineSegment(sketch, "E19.3.0.29", {"start": v(-6.48, -550) * mm, "end": v(6.48, -550) * mm});
            skPoint(sketch, "E19.6.0.29", {"position": v(9.48, -550) * mm});
            skPoint(sketch, "E19.7.0.29", {"position": v(-9.48, -556) * mm});
            skPoint(sketch, "E19.8.0.29", {"position": v(9.48, -556) * mm});
            skPoint(sketch, "E19.9.0.29", {"position": v(-9.48, -550) * mm});
            skPoint(sketch, "E19.10.0.29", {"position": v(0, -553) * mm});
            skArc(sketch, "E19.11.0.29", {"start": v(-9.48, -553) * mm, "mid": v(-8.6, -555.12) * mm, "end": v(-6.48, -556) * mm});
            skArc(sketch, "E19.15.0.29", {"start": v(-6.48, -550) * mm, "mid": v(-8.6, -550.88) * mm, "end": v(-9.48, -553) * mm});
            skArc(sketch, "E19.19.0.29", {"start": v(9.48, -553) * mm, "mid": v(8.6, -550.88) * mm, "end": v(6.48, -550) * mm});
            skArc(sketch, "E19.23.0.29", {"start": v(6.48, -556) * mm, "mid": v(8.6, -555.12) * mm, "end": v(9.48, -553) * mm});
            skLineSegment(sketch, "E19.0.0.30", {"start": v(-6.48, -541) * mm, "end": v(6.48, -541) * mm});
            skLineSegment(sketch, "E19.3.0.30", {"start": v(-6.48, -535) * mm, "end": v(6.48, -535) * mm});
            skPoint(sketch, "E19.6.0.30", {"position": v(9.48, -535) * mm});
            skPoint(sketch, "E19.7.0.30", {"position": v(-9.48, -541) * mm});
            skPoint(sketch, "E19.8.0.30", {"position": v(9.48, -541) * mm});
            skPoint(sketch, "E19.9.0.30", {"position": v(-9.48, -535) * mm});
            skPoint(sketch, "E19.10.0.30", {"position": v(0, -538) * mm});
            skArc(sketch, "E19.11.0.30", {"start": v(-9.48, -538) * mm, "mid": v(-8.6, -540.12) * mm, "end": v(-6.48, -541) * mm});
            skArc(sketch, "E19.15.0.30", {"start": v(-6.48, -535) * mm, "mid": v(-8.6, -535.88) * mm, "end": v(-9.48, -538) * mm});
            skArc(sketch, "E19.19.0.30", {"start": v(9.48, -538) * mm, "mid": v(8.6, -535.88) * mm, "end": v(6.48, -535) * mm});
            skArc(sketch, "E19.23.0.30", {"start": v(6.48, -541) * mm, "mid": v(8.6, -540.12) * mm, "end": v(9.48, -538) * mm});
            skLineSegment(sketch, "E19.0.0.31", {"start": v(-6.48, -526) * mm, "end": v(6.48, -526) * mm});
            skLineSegment(sketch, "E19.3.0.31", {"start": v(-6.48, -520) * mm, "end": v(6.48, -520) * mm});
            skPoint(sketch, "E19.6.0.31", {"position": v(9.48, -520) * mm});
            skPoint(sketch, "E19.7.0.31", {"position": v(-9.48, -526) * mm});
            skPoint(sketch, "E19.8.0.31", {"position": v(9.48, -526) * mm});
            skPoint(sketch, "E19.9.0.31", {"position": v(-9.48, -520) * mm});
            skPoint(sketch, "E19.10.0.31", {"position": v(0, -523) * mm});
            skArc(sketch, "E19.11.0.31", {"start": v(-9.48, -523) * mm, "mid": v(-8.6, -525.12) * mm, "end": v(-6.48, -526) * mm});
            skArc(sketch, "E19.15.0.31", {"start": v(-6.48, -520) * mm, "mid": v(-8.6, -520.88) * mm, "end": v(-9.48, -523) * mm});
            skArc(sketch, "E19.19.0.31", {"start": v(9.48, -523) * mm, "mid": v(8.6, -520.88) * mm, "end": v(6.48, -520) * mm});
            skArc(sketch, "E19.23.0.31", {"start": v(6.48, -526) * mm, "mid": v(8.6, -525.12) * mm, "end": v(9.48, -523) * mm});
            skLineSegment(sketch, "E19.0.0.32", {"start": v(-6.48, -511) * mm, "end": v(6.48, -511) * mm});
            skLineSegment(sketch, "E19.3.0.32", {"start": v(-6.48, -505) * mm, "end": v(6.48, -505) * mm});
            skPoint(sketch, "E19.6.0.32", {"position": v(9.48, -505) * mm});
            skPoint(sketch, "E19.7.0.32", {"position": v(-9.48, -511) * mm});
            skPoint(sketch, "E19.8.0.32", {"position": v(9.48, -511) * mm});
            skPoint(sketch, "E19.9.0.32", {"position": v(-9.48, -505) * mm});
            skPoint(sketch, "E19.10.0.32", {"position": v(0, -508) * mm});
            skArc(sketch, "E19.11.0.32", {"start": v(-9.48, -508) * mm, "mid": v(-8.6, -510.12) * mm, "end": v(-6.48, -511) * mm});
            skArc(sketch, "E19.15.0.32", {"start": v(-6.48, -505) * mm, "mid": v(-8.6, -505.88) * mm, "end": v(-9.48, -508) * mm});
            skArc(sketch, "E19.19.0.32", {"start": v(9.48, -508) * mm, "mid": v(8.6, -505.88) * mm, "end": v(6.48, -505) * mm});
            skArc(sketch, "E19.23.0.32", {"start": v(6.48, -511) * mm, "mid": v(8.6, -510.12) * mm, "end": v(9.48, -508) * mm});
            skLineSegment(sketch, "E19.0.0.33", {"start": v(-6.48, -496) * mm, "end": v(6.48, -496) * mm});
            skLineSegment(sketch, "E19.3.0.33", {"start": v(-6.48, -490) * mm, "end": v(6.48, -490) * mm});
            skPoint(sketch, "E19.6.0.33", {"position": v(9.48, -490) * mm});
            skPoint(sketch, "E19.7.0.33", {"position": v(-9.48, -496) * mm});
            skPoint(sketch, "E19.8.0.33", {"position": v(9.48, -496) * mm});
            skPoint(sketch, "E19.9.0.33", {"position": v(-9.48, -490) * mm});
            skPoint(sketch, "E19.10.0.33", {"position": v(0, -493) * mm});
            skArc(sketch, "E19.11.0.33", {"start": v(-9.48, -493) * mm, "mid": v(-8.6, -495.12) * mm, "end": v(-6.48, -496) * mm});
            skArc(sketch, "E19.15.0.33", {"start": v(-6.48, -490) * mm, "mid": v(-8.6, -490.88) * mm, "end": v(-9.48, -493) * mm});
            skArc(sketch, "E19.19.0.33", {"start": v(9.48, -493) * mm, "mid": v(8.6, -490.88) * mm, "end": v(6.48, -490) * mm});
            skArc(sketch, "E19.23.0.33", {"start": v(6.48, -496) * mm, "mid": v(8.6, -495.12) * mm, "end": v(9.48, -493) * mm});
            skLineSegment(sketch, "E19.0.0.34", {"start": v(-6.48, -481) * mm, "end": v(6.48, -481) * mm});
            skLineSegment(sketch, "E19.3.0.34", {"start": v(-6.48, -475) * mm, "end": v(6.48, -475) * mm});
            skPoint(sketch, "E19.6.0.34", {"position": v(9.48, -475) * mm});
            skPoint(sketch, "E19.7.0.34", {"position": v(-9.48, -481) * mm});
            skPoint(sketch, "E19.8.0.34", {"position": v(9.48, -481) * mm});
            skPoint(sketch, "E19.9.0.34", {"position": v(-9.48, -475) * mm});
            skPoint(sketch, "E19.10.0.34", {"position": v(0, -478) * mm});
            skArc(sketch, "E19.11.0.34", {"start": v(-9.48, -478) * mm, "mid": v(-8.6, -480.12) * mm, "end": v(-6.48, -481) * mm});
            skArc(sketch, "E19.15.0.34", {"start": v(-6.48, -475) * mm, "mid": v(-8.6, -475.88) * mm, "end": v(-9.48, -478) * mm});
            skArc(sketch, "E19.19.0.34", {"start": v(9.48, -478) * mm, "mid": v(8.6, -475.88) * mm, "end": v(6.48, -475) * mm});
            skArc(sketch, "E19.23.0.34", {"start": v(6.48, -481) * mm, "mid": v(8.6, -480.12) * mm, "end": v(9.48, -478) * mm});
            skLineSegment(sketch, "E19.0.0.35", {"start": v(-6.48, -466) * mm, "end": v(6.48, -466) * mm});
            skLineSegment(sketch, "E19.3.0.35", {"start": v(-6.48, -460) * mm, "end": v(6.48, -460) * mm});
            skPoint(sketch, "E19.6.0.35", {"position": v(9.48, -460) * mm});
            skPoint(sketch, "E19.7.0.35", {"position": v(-9.48, -466) * mm});
            skPoint(sketch, "E19.8.0.35", {"position": v(9.48, -466) * mm});
            skPoint(sketch, "E19.9.0.35", {"position": v(-9.48, -460) * mm});
            skPoint(sketch, "E19.10.0.35", {"position": v(0, -463) * mm});
            skArc(sketch, "E19.11.0.35", {"start": v(-9.48, -463) * mm, "mid": v(-8.6, -465.12) * mm, "end": v(-6.48, -466) * mm});
            skArc(sketch, "E19.15.0.35", {"start": v(-6.48, -460) * mm, "mid": v(-8.6, -460.88) * mm, "end": v(-9.48, -463) * mm});
            skArc(sketch, "E19.19.0.35", {"start": v(9.48, -463) * mm, "mid": v(8.6, -460.88) * mm, "end": v(6.48, -460) * mm});
            skArc(sketch, "E19.23.0.35", {"start": v(6.48, -466) * mm, "mid": v(8.6, -465.12) * mm, "end": v(9.48, -463) * mm});
            skLineSegment(sketch, "E19.0.0.36", {"start": v(-6.48, -451) * mm, "end": v(6.48, -451) * mm});
            skLineSegment(sketch, "E19.3.0.36", {"start": v(-6.48, -445) * mm, "end": v(6.48, -445) * mm});
            skPoint(sketch, "E19.6.0.36", {"position": v(9.48, -445) * mm});
            skPoint(sketch, "E19.7.0.36", {"position": v(-9.48, -451) * mm});
            skPoint(sketch, "E19.8.0.36", {"position": v(9.48, -451) * mm});
            skPoint(sketch, "E19.9.0.36", {"position": v(-9.48, -445) * mm});
            skPoint(sketch, "E19.10.0.36", {"position": v(0, -448) * mm});
            skArc(sketch, "E19.11.0.36", {"start": v(-9.48, -448) * mm, "mid": v(-8.6, -450.12) * mm, "end": v(-6.48, -451) * mm});
            skArc(sketch, "E19.15.0.36", {"start": v(-6.48, -445) * mm, "mid": v(-8.6, -445.88) * mm, "end": v(-9.48, -448) * mm});
            skArc(sketch, "E19.19.0.36", {"start": v(9.48, -448) * mm, "mid": v(8.6, -445.88) * mm, "end": v(6.48, -445) * mm});
            skArc(sketch, "E19.23.0.36", {"start": v(6.48, -451) * mm, "mid": v(8.6, -450.12) * mm, "end": v(9.48, -448) * mm});
            skLineSegment(sketch, "E19.0.0.37", {"start": v(-6.48, -436) * mm, "end": v(6.48, -436) * mm});
            skLineSegment(sketch, "E19.3.0.37", {"start": v(-6.48, -430) * mm, "end": v(6.48, -430) * mm});
            skPoint(sketch, "E19.6.0.37", {"position": v(9.48, -430) * mm});
            skPoint(sketch, "E19.7.0.37", {"position": v(-9.48, -436) * mm});
            skPoint(sketch, "E19.8.0.37", {"position": v(9.48, -436) * mm});
            skPoint(sketch, "E19.9.0.37", {"position": v(-9.48, -430) * mm});
            skPoint(sketch, "E19.10.0.37", {"position": v(0, -433) * mm});
            skArc(sketch, "E19.11.0.37", {"start": v(-9.48, -433) * mm, "mid": v(-8.6, -435.12) * mm, "end": v(-6.48, -436) * mm});
            skArc(sketch, "E19.15.0.37", {"start": v(-6.48, -430) * mm, "mid": v(-8.6, -430.88) * mm, "end": v(-9.48, -433) * mm});
            skArc(sketch, "E19.19.0.37", {"start": v(9.48, -433) * mm, "mid": v(8.6, -430.88) * mm, "end": v(6.48, -430) * mm});
            skArc(sketch, "E19.23.0.37", {"start": v(6.48, -436) * mm, "mid": v(8.6, -435.12) * mm, "end": v(9.48, -433) * mm});
            skLineSegment(sketch, "E19.0.0.38", {"start": v(-6.48, -421) * mm, "end": v(6.48, -421) * mm});
            skLineSegment(sketch, "E19.3.0.38", {"start": v(-6.48, -415) * mm, "end": v(6.48, -415) * mm});
            skPoint(sketch, "E19.6.0.38", {"position": v(9.48, -415) * mm});
            skPoint(sketch, "E19.7.0.38", {"position": v(-9.48, -421) * mm});
            skPoint(sketch, "E19.8.0.38", {"position": v(9.48, -421) * mm});
            skPoint(sketch, "E19.9.0.38", {"position": v(-9.48, -415) * mm});
            skPoint(sketch, "E19.10.0.38", {"position": v(0, -418) * mm});
            skArc(sketch, "E19.11.0.38", {"start": v(-9.48, -418) * mm, "mid": v(-8.6, -420.12) * mm, "end": v(-6.48, -421) * mm});
            skArc(sketch, "E19.15.0.38", {"start": v(-6.48, -415) * mm, "mid": v(-8.6, -415.88) * mm, "end": v(-9.48, -418) * mm});
            skArc(sketch, "E19.19.0.38", {"start": v(9.48, -418) * mm, "mid": v(8.6, -415.88) * mm, "end": v(6.48, -415) * mm});
            skArc(sketch, "E19.23.0.38", {"start": v(6.48, -421) * mm, "mid": v(8.6, -420.12) * mm, "end": v(9.48, -418) * mm});
            skLineSegment(sketch, "E19.0.0.39", {"start": v(-6.48, -406) * mm, "end": v(6.48, -406) * mm});
            skLineSegment(sketch, "E19.3.0.39", {"start": v(-6.48, -400) * mm, "end": v(6.48, -400) * mm});
            skPoint(sketch, "E19.6.0.39", {"position": v(9.48, -400) * mm});
            skPoint(sketch, "E19.7.0.39", {"position": v(-9.48, -406) * mm});
            skPoint(sketch, "E19.8.0.39", {"position": v(9.48, -406) * mm});
            skPoint(sketch, "E19.9.0.39", {"position": v(-9.48, -400) * mm});
            skPoint(sketch, "E19.10.0.39", {"position": v(0, -403) * mm});
            skArc(sketch, "E19.11.0.39", {"start": v(-9.48, -403) * mm, "mid": v(-8.6, -405.12) * mm, "end": v(-6.48, -406) * mm});
            skArc(sketch, "E19.15.0.39", {"start": v(-6.48, -400) * mm, "mid": v(-8.6, -400.88) * mm, "end": v(-9.48, -403) * mm});
            skArc(sketch, "E19.19.0.39", {"start": v(9.48, -403) * mm, "mid": v(8.6, -400.88) * mm, "end": v(6.48, -400) * mm});
            skArc(sketch, "E19.23.0.39", {"start": v(6.48, -406) * mm, "mid": v(8.6, -405.12) * mm, "end": v(9.48, -403) * mm});
            skLineSegment(sketch, "E19.0.0.40", {"start": v(-6.48, -391) * mm, "end": v(6.48, -391) * mm});
            skLineSegment(sketch, "E19.3.0.40", {"start": v(-6.48, -385) * mm, "end": v(6.48, -385) * mm});
            skPoint(sketch, "E19.6.0.40", {"position": v(9.48, -385) * mm});
            skPoint(sketch, "E19.7.0.40", {"position": v(-9.48, -391) * mm});
            skPoint(sketch, "E19.8.0.40", {"position": v(9.48, -391) * mm});
            skPoint(sketch, "E19.9.0.40", {"position": v(-9.48, -385) * mm});
            skPoint(sketch, "E19.10.0.40", {"position": v(0, -388) * mm});
            skArc(sketch, "E19.11.0.40", {"start": v(-9.48, -388) * mm, "mid": v(-8.6, -390.12) * mm, "end": v(-6.48, -391) * mm});
            skArc(sketch, "E19.15.0.40", {"start": v(-6.48, -385) * mm, "mid": v(-8.6, -385.88) * mm, "end": v(-9.48, -388) * mm});
            skArc(sketch, "E19.19.0.40", {"start": v(9.48, -388) * mm, "mid": v(8.6, -385.88) * mm, "end": v(6.48, -385) * mm});
            skArc(sketch, "E19.23.0.40", {"start": v(6.48, -391) * mm, "mid": v(8.6, -390.12) * mm, "end": v(9.48, -388) * mm});
            skLineSegment(sketch, "E19.0.0.41", {"start": v(-6.48, -376) * mm, "end": v(6.48, -376) * mm});
            skLineSegment(sketch, "E19.3.0.41", {"start": v(-6.48, -370) * mm, "end": v(6.48, -370) * mm});
            skPoint(sketch, "E19.6.0.41", {"position": v(9.48, -370) * mm});
            skPoint(sketch, "E19.7.0.41", {"position": v(-9.48, -376) * mm});
            skPoint(sketch, "E19.8.0.41", {"position": v(9.48, -376) * mm});
            skPoint(sketch, "E19.9.0.41", {"position": v(-9.48, -370) * mm});
            skPoint(sketch, "E19.10.0.41", {"position": v(0, -373) * mm});
            skArc(sketch, "E19.11.0.41", {"start": v(-9.48, -373) * mm, "mid": v(-8.6, -375.12) * mm, "end": v(-6.48, -376) * mm});
            skArc(sketch, "E19.15.0.41", {"start": v(-6.48, -370) * mm, "mid": v(-8.6, -370.88) * mm, "end": v(-9.48, -373) * mm});
            skArc(sketch, "E19.19.0.41", {"start": v(9.48, -373) * mm, "mid": v(8.6, -370.88) * mm, "end": v(6.48, -370) * mm});
            skArc(sketch, "E19.23.0.41", {"start": v(6.48, -376) * mm, "mid": v(8.6, -375.12) * mm, "end": v(9.48, -373) * mm});
            skLineSegment(sketch, "E19.0.0.42", {"start": v(-6.48, -361) * mm, "end": v(6.48, -361) * mm});
            skLineSegment(sketch, "E19.3.0.42", {"start": v(-6.48, -355) * mm, "end": v(6.48, -355) * mm});
            skPoint(sketch, "E19.6.0.42", {"position": v(9.48, -355) * mm});
            skPoint(sketch, "E19.7.0.42", {"position": v(-9.48, -361) * mm});
            skPoint(sketch, "E19.8.0.42", {"position": v(9.48, -361) * mm});
            skPoint(sketch, "E19.9.0.42", {"position": v(-9.48, -355) * mm});
            skPoint(sketch, "E19.10.0.42", {"position": v(0, -358) * mm});
            skArc(sketch, "E19.11.0.42", {"start": v(-9.48, -358) * mm, "mid": v(-8.6, -360.12) * mm, "end": v(-6.48, -361) * mm});
            skArc(sketch, "E19.15.0.42", {"start": v(-6.48, -355) * mm, "mid": v(-8.6, -355.88) * mm, "end": v(-9.48, -358) * mm});
            skArc(sketch, "E19.19.0.42", {"start": v(9.48, -358) * mm, "mid": v(8.6, -355.88) * mm, "end": v(6.48, -355) * mm});
            skArc(sketch, "E19.23.0.42", {"start": v(6.48, -361) * mm, "mid": v(8.6, -360.12) * mm, "end": v(9.48, -358) * mm});
            skLineSegment(sketch, "E19.0.0.43", {"start": v(-6.48, -346) * mm, "end": v(6.48, -346) * mm});
            skLineSegment(sketch, "E19.3.0.43", {"start": v(-6.48, -340) * mm, "end": v(6.48, -340) * mm});
            skPoint(sketch, "E19.6.0.43", {"position": v(9.48, -340) * mm});
            skPoint(sketch, "E19.7.0.43", {"position": v(-9.48, -346) * mm});
            skPoint(sketch, "E19.8.0.43", {"position": v(9.48, -346) * mm});
            skPoint(sketch, "E19.9.0.43", {"position": v(-9.48, -340) * mm});
            skPoint(sketch, "E19.10.0.43", {"position": v(0, -343) * mm});
            skArc(sketch, "E19.11.0.43", {"start": v(-9.48, -343) * mm, "mid": v(-8.6, -345.12) * mm, "end": v(-6.48, -346) * mm});
            skArc(sketch, "E19.15.0.43", {"start": v(-6.48, -340) * mm, "mid": v(-8.6, -340.88) * mm, "end": v(-9.48, -343) * mm});
            skArc(sketch, "E19.19.0.43", {"start": v(9.48, -343) * mm, "mid": v(8.6, -340.88) * mm, "end": v(6.48, -340) * mm});
            skArc(sketch, "E19.23.0.43", {"start": v(6.48, -346) * mm, "mid": v(8.6, -345.12) * mm, "end": v(9.48, -343) * mm});
            skLineSegment(sketch, "E19.0.0.44", {"start": v(-6.48, -331) * mm, "end": v(6.48, -331) * mm});
            skLineSegment(sketch, "E19.3.0.44", {"start": v(-6.48, -325) * mm, "end": v(6.48, -325) * mm});
            skPoint(sketch, "E19.6.0.44", {"position": v(9.48, -325) * mm});
            skPoint(sketch, "E19.7.0.44", {"position": v(-9.48, -331) * mm});
            skPoint(sketch, "E19.8.0.44", {"position": v(9.48, -331) * mm});
            skPoint(sketch, "E19.9.0.44", {"position": v(-9.48, -325) * mm});
            skPoint(sketch, "E19.10.0.44", {"position": v(0, -328) * mm});
            skArc(sketch, "E19.11.0.44", {"start": v(-9.48, -328) * mm, "mid": v(-8.6, -330.12) * mm, "end": v(-6.48, -331) * mm});
            skArc(sketch, "E19.15.0.44", {"start": v(-6.48, -325) * mm, "mid": v(-8.6, -325.88) * mm, "end": v(-9.48, -328) * mm});
            skArc(sketch, "E19.19.0.44", {"start": v(9.48, -328) * mm, "mid": v(8.6, -325.88) * mm, "end": v(6.48, -325) * mm});
            skArc(sketch, "E19.23.0.44", {"start": v(6.48, -331) * mm, "mid": v(8.6, -330.12) * mm, "end": v(9.48, -328) * mm});
            skLineSegment(sketch, "E19.0.0.45", {"start": v(-6.48, -316) * mm, "end": v(6.48, -316) * mm});
            skLineSegment(sketch, "E19.3.0.45", {"start": v(-6.48, -310) * mm, "end": v(6.48, -310) * mm});
            skPoint(sketch, "E19.6.0.45", {"position": v(9.48, -310) * mm});
            skPoint(sketch, "E19.7.0.45", {"position": v(-9.48, -316) * mm});
            skPoint(sketch, "E19.8.0.45", {"position": v(9.48, -316) * mm});
            skPoint(sketch, "E19.9.0.45", {"position": v(-9.48, -310) * mm});
            skPoint(sketch, "E19.10.0.45", {"position": v(0, -313) * mm});
            skArc(sketch, "E19.11.0.45", {"start": v(-9.48, -313) * mm, "mid": v(-8.6, -315.12) * mm, "end": v(-6.48, -316) * mm});
            skArc(sketch, "E19.15.0.45", {"start": v(-6.48, -310) * mm, "mid": v(-8.6, -310.88) * mm, "end": v(-9.48, -313) * mm});
            skArc(sketch, "E19.19.0.45", {"start": v(9.48, -313) * mm, "mid": v(8.6, -310.88) * mm, "end": v(6.48, -310) * mm});
            skArc(sketch, "E19.23.0.45", {"start": v(6.48, -316) * mm, "mid": v(8.6, -315.12) * mm, "end": v(9.48, -313) * mm});
            skLineSegment(sketch, "E19.0.0.46", {"start": v(-6.48, -301) * mm, "end": v(6.48, -301) * mm});
            skLineSegment(sketch, "E19.3.0.46", {"start": v(-6.48, -295) * mm, "end": v(6.48, -295) * mm});
            skPoint(sketch, "E19.6.0.46", {"position": v(9.48, -295) * mm});
            skPoint(sketch, "E19.7.0.46", {"position": v(-9.48, -301) * mm});
            skPoint(sketch, "E19.8.0.46", {"position": v(9.48, -301) * mm});
            skPoint(sketch, "E19.9.0.46", {"position": v(-9.48, -295) * mm});
            skPoint(sketch, "E19.10.0.46", {"position": v(0, -298) * mm});
            skArc(sketch, "E19.11.0.46", {"start": v(-9.48, -298) * mm, "mid": v(-8.6, -300.12) * mm, "end": v(-6.48, -301) * mm});
            skArc(sketch, "E19.15.0.46", {"start": v(-6.48, -295) * mm, "mid": v(-8.6, -295.88) * mm, "end": v(-9.48, -298) * mm});
            skArc(sketch, "E19.19.0.46", {"start": v(9.48, -298) * mm, "mid": v(8.6, -295.88) * mm, "end": v(6.48, -295) * mm});
            skArc(sketch, "E19.23.0.46", {"start": v(6.48, -301) * mm, "mid": v(8.6, -300.12) * mm, "end": v(9.48, -298) * mm});
            skLineSegment(sketch, "E19.0.0.47", {"start": v(-6.48, -286) * mm, "end": v(6.48, -286) * mm});
            skLineSegment(sketch, "E19.3.0.47", {"start": v(-6.48, -280) * mm, "end": v(6.48, -280) * mm});
            skPoint(sketch, "E19.6.0.47", {"position": v(9.48, -280) * mm});
            skPoint(sketch, "E19.7.0.47", {"position": v(-9.48, -286) * mm});
            skPoint(sketch, "E19.8.0.47", {"position": v(9.48, -286) * mm});
            skPoint(sketch, "E19.9.0.47", {"position": v(-9.48, -280) * mm});
            skPoint(sketch, "E19.10.0.47", {"position": v(0, -283) * mm});
            skArc(sketch, "E19.11.0.47", {"start": v(-9.48, -283) * mm, "mid": v(-8.6, -285.12) * mm, "end": v(-6.48, -286) * mm});
            skArc(sketch, "E19.15.0.47", {"start": v(-6.48, -280) * mm, "mid": v(-8.6, -280.88) * mm, "end": v(-9.48, -283) * mm});
            skArc(sketch, "E19.19.0.47", {"start": v(9.48, -283) * mm, "mid": v(8.6, -280.88) * mm, "end": v(6.48, -280) * mm});
            skArc(sketch, "E19.23.0.47", {"start": v(6.48, -286) * mm, "mid": v(8.6, -285.12) * mm, "end": v(9.48, -283) * mm});
            skLineSegment(sketch, "E19.0.0.48", {"start": v(-6.48, -271) * mm, "end": v(6.48, -271) * mm});
            skLineSegment(sketch, "E19.3.0.48", {"start": v(-6.48, -265) * mm, "end": v(6.48, -265) * mm});
            skPoint(sketch, "E19.6.0.48", {"position": v(9.48, -265) * mm});
            skPoint(sketch, "E19.7.0.48", {"position": v(-9.48, -271) * mm});
            skPoint(sketch, "E19.8.0.48", {"position": v(9.48, -271) * mm});
            skPoint(sketch, "E19.9.0.48", {"position": v(-9.48, -265) * mm});
            skPoint(sketch, "E19.10.0.48", {"position": v(0, -268) * mm});
            skArc(sketch, "E19.11.0.48", {"start": v(-9.48, -268) * mm, "mid": v(-8.6, -270.12) * mm, "end": v(-6.48, -271) * mm});
            skArc(sketch, "E19.15.0.48", {"start": v(-6.48, -265) * mm, "mid": v(-8.6, -265.88) * mm, "end": v(-9.48, -268) * mm});
            skArc(sketch, "E19.19.0.48", {"start": v(9.48, -268) * mm, "mid": v(8.6, -265.88) * mm, "end": v(6.48, -265) * mm});
            skArc(sketch, "E19.23.0.48", {"start": v(6.48, -271) * mm, "mid": v(8.6, -270.12) * mm, "end": v(9.48, -268) * mm});
            skLineSegment(sketch, "E19.0.0.49", {"start": v(-6.48, -256) * mm, "end": v(6.48, -256) * mm});
            skLineSegment(sketch, "E19.3.0.49", {"start": v(-6.48, -250) * mm, "end": v(6.48, -250) * mm});
            skPoint(sketch, "E19.6.0.49", {"position": v(9.48, -250) * mm});
            skPoint(sketch, "E19.7.0.49", {"position": v(-9.48, -256) * mm});
            skPoint(sketch, "E19.8.0.49", {"position": v(9.48, -256) * mm});
            skPoint(sketch, "E19.9.0.49", {"position": v(-9.48, -250) * mm});
            skPoint(sketch, "E19.10.0.49", {"position": v(0, -253) * mm});
            skArc(sketch, "E19.11.0.49", {"start": v(-9.48, -253) * mm, "mid": v(-8.6, -255.12) * mm, "end": v(-6.48, -256) * mm});
            skArc(sketch, "E19.15.0.49", {"start": v(-6.48, -250) * mm, "mid": v(-8.6, -250.88) * mm, "end": v(-9.48, -253) * mm});
            skArc(sketch, "E19.19.0.49", {"start": v(9.48, -253) * mm, "mid": v(8.6, -250.88) * mm, "end": v(6.48, -250) * mm});
            skArc(sketch, "E19.23.0.49", {"start": v(6.48, -256) * mm, "mid": v(8.6, -255.12) * mm, "end": v(9.48, -253) * mm});
            skLineSegment(sketch, "E20.0.0.50", {"start": v(-6.48, -241) * mm, "end": v(6.48, -241) * mm});
            skLineSegment(sketch, "E20.3.0.50", {"start": v(-6.48, -235) * mm, "end": v(6.48, -235) * mm});
            skPoint(sketch, "E20.6.0.50", {"position": v(9.48, -235) * mm});
            skPoint(sketch, "E20.7.0.50", {"position": v(-9.48, -241) * mm});
            skPoint(sketch, "E20.8.0.50", {"position": v(9.48, -241) * mm});
            skPoint(sketch, "E20.9.0.50", {"position": v(-9.48, -235) * mm});
            skPoint(sketch, "E20.10.0.50", {"position": v(0, -238) * mm});
            skArc(sketch, "E20.11.0.50", {"start": v(-9.48, -238) * mm, "mid": v(-8.6, -240.12) * mm, "end": v(-6.48, -241) * mm});
            skArc(sketch, "E20.15.0.50", {"start": v(-6.48, -235) * mm, "mid": v(-8.6, -235.88) * mm, "end": v(-9.48, -238) * mm});
            skArc(sketch, "E20.19.0.50", {"start": v(9.48, -238) * mm, "mid": v(8.6, -235.88) * mm, "end": v(6.48, -235) * mm});
            skArc(sketch, "E20.23.0.50", {"start": v(6.48, -241) * mm, "mid": v(8.6, -240.12) * mm, "end": v(9.48, -238) * mm});
            skLineSegment(sketch, "E20.0.0.51", {"start": v(-6.48, -226) * mm, "end": v(6.48, -226) * mm});
            skLineSegment(sketch, "E20.3.0.51", {"start": v(-6.48, -220) * mm, "end": v(6.48, -220) * mm});
            skPoint(sketch, "E20.6.0.51", {"position": v(9.48, -220) * mm});
            skPoint(sketch, "E20.7.0.51", {"position": v(-9.48, -226) * mm});
            skPoint(sketch, "E20.8.0.51", {"position": v(9.48, -226) * mm});
            skPoint(sketch, "E20.9.0.51", {"position": v(-9.48, -220) * mm});
            skPoint(sketch, "E20.10.0.51", {"position": v(0, -223) * mm});
            skArc(sketch, "E20.11.0.51", {"start": v(-9.48, -223) * mm, "mid": v(-8.6, -225.12) * mm, "end": v(-6.48, -226) * mm});
            skArc(sketch, "E20.15.0.51", {"start": v(-6.48, -220) * mm, "mid": v(-8.6, -220.88) * mm, "end": v(-9.48, -223) * mm});
            skArc(sketch, "E20.19.0.51", {"start": v(9.48, -223) * mm, "mid": v(8.6, -220.88) * mm, "end": v(6.48, -220) * mm});
            skArc(sketch, "E20.23.0.51", {"start": v(6.48, -226) * mm, "mid": v(8.6, -225.12) * mm, "end": v(9.48, -223) * mm});
            skLineSegment(sketch, "E20.0.0.52", {"start": v(-6.48, -211) * mm, "end": v(6.48, -211) * mm});
            skLineSegment(sketch, "E20.3.0.52", {"start": v(-6.48, -205) * mm, "end": v(6.48, -205) * mm});
            skPoint(sketch, "E20.6.0.52", {"position": v(9.48, -205) * mm});
            skPoint(sketch, "E20.7.0.52", {"position": v(-9.48, -211) * mm});
            skPoint(sketch, "E20.8.0.52", {"position": v(9.48, -211) * mm});
            skPoint(sketch, "E20.9.0.52", {"position": v(-9.48, -205) * mm});
            skPoint(sketch, "E20.10.0.52", {"position": v(0, -208) * mm});
            skArc(sketch, "E20.11.0.52", {"start": v(-9.48, -208) * mm, "mid": v(-8.6, -210.12) * mm, "end": v(-6.48, -211) * mm});
            skArc(sketch, "E20.15.0.52", {"start": v(-6.48, -205) * mm, "mid": v(-8.6, -205.88) * mm, "end": v(-9.48, -208) * mm});
            skArc(sketch, "E20.19.0.52", {"start": v(9.48, -208) * mm, "mid": v(8.6, -205.88) * mm, "end": v(6.48, -205) * mm});
            skArc(sketch, "E20.23.0.52", {"start": v(6.48, -211) * mm, "mid": v(8.6, -210.12) * mm, "end": v(9.48, -208) * mm});
            skLineSegment(sketch, "E20.0.0.53", {"start": v(-6.48, -196) * mm, "end": v(6.48, -196) * mm});
            skLineSegment(sketch, "E20.3.0.53", {"start": v(-6.48, -190) * mm, "end": v(6.48, -190) * mm});
            skPoint(sketch, "E20.6.0.53", {"position": v(9.48, -190) * mm});
            skPoint(sketch, "E20.7.0.53", {"position": v(-9.48, -196) * mm});
            skPoint(sketch, "E20.8.0.53", {"position": v(9.48, -196) * mm});
            skPoint(sketch, "E20.9.0.53", {"position": v(-9.48, -190) * mm});
            skPoint(sketch, "E20.10.0.53", {"position": v(0, -193) * mm});
            skArc(sketch, "E20.11.0.53", {"start": v(-9.48, -193) * mm, "mid": v(-8.6, -195.12) * mm, "end": v(-6.48, -196) * mm});
            skArc(sketch, "E20.15.0.53", {"start": v(-6.48, -190) * mm, "mid": v(-8.6, -190.88) * mm, "end": v(-9.48, -193) * mm});
            skArc(sketch, "E20.19.0.53", {"start": v(9.48, -193) * mm, "mid": v(8.6, -190.88) * mm, "end": v(6.48, -190) * mm});
            skArc(sketch, "E20.23.0.53", {"start": v(6.48, -196) * mm, "mid": v(8.6, -195.12) * mm, "end": v(9.48, -193) * mm});
            skLineSegment(sketch, "E20.0.0.54", {"start": v(-6.48, -181) * mm, "end": v(6.48, -181) * mm});
            skLineSegment(sketch, "E20.3.0.54", {"start": v(-6.48, -175) * mm, "end": v(6.48, -175) * mm});
            skPoint(sketch, "E20.6.0.54", {"position": v(9.48, -175) * mm});
            skPoint(sketch, "E20.7.0.54", {"position": v(-9.48, -181) * mm});
            skPoint(sketch, "E20.8.0.54", {"position": v(9.48, -181) * mm});
            skPoint(sketch, "E20.9.0.54", {"position": v(-9.48, -175) * mm});
            skPoint(sketch, "E20.10.0.54", {"position": v(0, -178) * mm});
            skArc(sketch, "E20.11.0.54", {"start": v(-9.48, -178) * mm, "mid": v(-8.6, -180.12) * mm, "end": v(-6.48, -181) * mm});
            skArc(sketch, "E20.15.0.54", {"start": v(-6.48, -175) * mm, "mid": v(-8.6, -175.88) * mm, "end": v(-9.48, -178) * mm});
            skArc(sketch, "E20.19.0.54", {"start": v(9.48, -178) * mm, "mid": v(8.6, -175.88) * mm, "end": v(6.48, -175) * mm});
            skArc(sketch, "E20.23.0.54", {"start": v(6.48, -181) * mm, "mid": v(8.6, -180.12) * mm, "end": v(9.48, -178) * mm});
            skLineSegment(sketch, "E20.0.0.55", {"start": v(-6.48, -166) * mm, "end": v(6.48, -166) * mm});
            skLineSegment(sketch, "E20.3.0.55", {"start": v(-6.48, -160) * mm, "end": v(6.48, -160) * mm});
            skPoint(sketch, "E20.6.0.55", {"position": v(9.48, -160) * mm});
            skPoint(sketch, "E20.7.0.55", {"position": v(-9.48, -166) * mm});
            skPoint(sketch, "E20.8.0.55", {"position": v(9.48, -166) * mm});
            skPoint(sketch, "E20.9.0.55", {"position": v(-9.48, -160) * mm});
            skPoint(sketch, "E20.10.0.55", {"position": v(0, -163) * mm});
            skArc(sketch, "E20.11.0.55", {"start": v(-9.48, -163) * mm, "mid": v(-8.6, -165.12) * mm, "end": v(-6.48, -166) * mm});
            skArc(sketch, "E20.15.0.55", {"start": v(-6.48, -160) * mm, "mid": v(-8.6, -160.88) * mm, "end": v(-9.48, -163) * mm});
            skArc(sketch, "E20.19.0.55", {"start": v(9.48, -163) * mm, "mid": v(8.6, -160.88) * mm, "end": v(6.48, -160) * mm});
            skArc(sketch, "E20.23.0.55", {"start": v(6.48, -166) * mm, "mid": v(8.6, -165.12) * mm, "end": v(9.48, -163) * mm});
            skLineSegment(sketch, "E20.0.0.56", {"start": v(-6.48, -151) * mm, "end": v(6.48, -151) * mm});
            skLineSegment(sketch, "E20.3.0.56", {"start": v(-6.48, -145) * mm, "end": v(6.48, -145) * mm});
            skPoint(sketch, "E20.6.0.56", {"position": v(9.48, -145) * mm});
            skPoint(sketch, "E20.7.0.56", {"position": v(-9.48, -151) * mm});
            skPoint(sketch, "E20.8.0.56", {"position": v(9.48, -151) * mm});
            skPoint(sketch, "E20.9.0.56", {"position": v(-9.48, -145) * mm});
            skPoint(sketch, "E20.10.0.56", {"position": v(0, -148) * mm});
            skArc(sketch, "E20.11.0.56", {"start": v(-9.48, -148) * mm, "mid": v(-8.6, -150.12) * mm, "end": v(-6.48, -151) * mm});
            skArc(sketch, "E20.15.0.56", {"start": v(-6.48, -145) * mm, "mid": v(-8.6, -145.88) * mm, "end": v(-9.48, -148) * mm});
            skArc(sketch, "E20.19.0.56", {"start": v(9.48, -148) * mm, "mid": v(8.6, -145.88) * mm, "end": v(6.48, -145) * mm});
            skArc(sketch, "E20.23.0.56", {"start": v(6.48, -151) * mm, "mid": v(8.6, -150.12) * mm, "end": v(9.48, -148) * mm});
            skLineSegment(sketch, "E20.0.0.57", {"start": v(-6.48, -136) * mm, "end": v(6.48, -136) * mm});
            skLineSegment(sketch, "E20.3.0.57", {"start": v(-6.48, -130) * mm, "end": v(6.48, -130) * mm});
            skPoint(sketch, "E20.6.0.57", {"position": v(9.48, -130) * mm});
            skPoint(sketch, "E20.7.0.57", {"position": v(-9.48, -136) * mm});
            skPoint(sketch, "E20.8.0.57", {"position": v(9.48, -136) * mm});
            skPoint(sketch, "E20.9.0.57", {"position": v(-9.48, -130) * mm});
            skPoint(sketch, "E20.10.0.57", {"position": v(0, -133) * mm});
            skArc(sketch, "E20.11.0.57", {"start": v(-9.48, -133) * mm, "mid": v(-8.6, -135.12) * mm, "end": v(-6.48, -136) * mm});
            skArc(sketch, "E20.15.0.57", {"start": v(-6.48, -130) * mm, "mid": v(-8.6, -130.88) * mm, "end": v(-9.48, -133) * mm});
            skArc(sketch, "E20.19.0.57", {"start": v(9.48, -133) * mm, "mid": v(8.6, -130.88) * mm, "end": v(6.48, -130) * mm});
            skArc(sketch, "E20.23.0.57", {"start": v(6.48, -136) * mm, "mid": v(8.6, -135.12) * mm, "end": v(9.48, -133) * mm});
            skLineSegment(sketch, "E20.0.0.58", {"start": v(-6.48, -121) * mm, "end": v(6.48, -121) * mm});
            skLineSegment(sketch, "E20.3.0.58", {"start": v(-6.48, -115) * mm, "end": v(6.48, -115) * mm});
            skPoint(sketch, "E20.6.0.58", {"position": v(9.48, -115) * mm});
            skPoint(sketch, "E20.7.0.58", {"position": v(-9.48, -121) * mm});
            skPoint(sketch, "E20.8.0.58", {"position": v(9.48, -121) * mm});
            skPoint(sketch, "E20.9.0.58", {"position": v(-9.48, -115) * mm});
            skPoint(sketch, "E20.10.0.58", {"position": v(0, -118) * mm});
            skArc(sketch, "E20.11.0.58", {"start": v(-9.48, -118) * mm, "mid": v(-8.6, -120.12) * mm, "end": v(-6.48, -121) * mm});
            skArc(sketch, "E20.15.0.58", {"start": v(-6.48, -115) * mm, "mid": v(-8.6, -115.88) * mm, "end": v(-9.48, -118) * mm});
            skArc(sketch, "E20.19.0.58", {"start": v(9.48, -118) * mm, "mid": v(8.6, -115.88) * mm, "end": v(6.48, -115) * mm});
            skArc(sketch, "E20.23.0.58", {"start": v(6.48, -121) * mm, "mid": v(8.6, -120.12) * mm, "end": v(9.48, -118) * mm});
            skLineSegment(sketch, "E20.0.0.59", {"start": v(-6.48, -106) * mm, "end": v(6.48, -106) * mm});
            skLineSegment(sketch, "E20.3.0.59", {"start": v(-6.48, -100) * mm, "end": v(6.48, -100) * mm});
            skPoint(sketch, "E20.6.0.59", {"position": v(9.48, -100) * mm});
            skPoint(sketch, "E20.7.0.59", {"position": v(-9.48, -106) * mm});
            skPoint(sketch, "E20.8.0.59", {"position": v(9.48, -106) * mm});
            skPoint(sketch, "E20.9.0.59", {"position": v(-9.48, -100) * mm});
            skPoint(sketch, "E20.10.0.59", {"position": v(0, -103) * mm});
            skArc(sketch, "E20.11.0.59", {"start": v(-9.48, -103) * mm, "mid": v(-8.6, -105.12) * mm, "end": v(-6.48, -106) * mm});
            skArc(sketch, "E20.15.0.59", {"start": v(-6.48, -100) * mm, "mid": v(-8.6, -100.88) * mm, "end": v(-9.48, -103) * mm});
            skArc(sketch, "E20.19.0.59", {"start": v(9.48, -103) * mm, "mid": v(8.6, -100.88) * mm, "end": v(6.48, -100) * mm});
            skArc(sketch, "E20.23.0.59", {"start": v(6.48, -106) * mm, "mid": v(8.6, -105.12) * mm, "end": v(9.48, -103) * mm});
            skLineSegment(sketch, "E21.0.0.60", {"start": v(-6.48, -91) * mm, "end": v(6.48, -91) * mm});
            skLineSegment(sketch, "E21.3.0.60", {"start": v(-6.48, -85) * mm, "end": v(6.48, -85) * mm});
            skPoint(sketch, "E21.6.0.60", {"position": v(9.48, -85) * mm});
            skPoint(sketch, "E21.7.0.60", {"position": v(-9.48, -91) * mm});
            skPoint(sketch, "E21.8.0.60", {"position": v(9.48, -91) * mm});
            skPoint(sketch, "E21.9.0.60", {"position": v(-9.48, -85) * mm});
            skPoint(sketch, "E21.10.0.60", {"position": v(0, -88) * mm});
            skArc(sketch, "E21.11.0.60", {"start": v(-9.48, -88) * mm, "mid": v(-8.6, -90.12) * mm, "end": v(-6.48, -91) * mm});
            skArc(sketch, "E21.15.0.60", {"start": v(-6.48, -85) * mm, "mid": v(-8.6, -85.88) * mm, "end": v(-9.48, -88) * mm});
            skArc(sketch, "E21.19.0.60", {"start": v(9.48, -88) * mm, "mid": v(8.6, -85.88) * mm, "end": v(6.48, -85) * mm});
            skArc(sketch, "E21.23.0.60", {"start": v(6.48, -91) * mm, "mid": v(8.6, -90.12) * mm, "end": v(9.48, -88) * mm});
            skLineSegment(sketch, "E21.0.0.61", {"start": v(-6.48, -76) * mm, "end": v(6.48, -76) * mm});
            skLineSegment(sketch, "E21.3.0.61", {"start": v(-6.48, -70) * mm, "end": v(6.48, -70) * mm});
            skPoint(sketch, "E21.6.0.61", {"position": v(9.48, -70) * mm});
            skPoint(sketch, "E21.7.0.61", {"position": v(-9.48, -76) * mm});
            skPoint(sketch, "E21.8.0.61", {"position": v(9.48, -76) * mm});
            skPoint(sketch, "E21.9.0.61", {"position": v(-9.48, -70) * mm});
            skPoint(sketch, "E21.10.0.61", {"position": v(0, -73) * mm});
            skArc(sketch, "E21.11.0.61", {"start": v(-9.48, -73) * mm, "mid": v(-8.6, -75.12) * mm, "end": v(-6.48, -76) * mm});
            skArc(sketch, "E21.15.0.61", {"start": v(-6.48, -70) * mm, "mid": v(-8.6, -70.88) * mm, "end": v(-9.48, -73) * mm});
            skArc(sketch, "E21.19.0.61", {"start": v(9.48, -73) * mm, "mid": v(8.6, -70.88) * mm, "end": v(6.48, -70) * mm});
            skArc(sketch, "E21.23.0.61", {"start": v(6.48, -76) * mm, "mid": v(8.6, -75.12) * mm, "end": v(9.48, -73) * mm});
            skLineSegment(sketch, "E21.0.0.62", {"start": v(-6.48, -61) * mm, "end": v(6.48, -61) * mm});
            skLineSegment(sketch, "E21.3.0.62", {"start": v(-6.48, -55) * mm, "end": v(6.48, -55) * mm});
            skPoint(sketch, "E21.6.0.62", {"position": v(9.48, -55) * mm});
            skPoint(sketch, "E21.7.0.62", {"position": v(-9.48, -61) * mm});
            skPoint(sketch, "E21.8.0.62", {"position": v(9.48, -61) * mm});
            skPoint(sketch, "E21.9.0.62", {"position": v(-9.48, -55) * mm});
            skPoint(sketch, "E21.10.0.62", {"position": v(0, -58) * mm});
            skArc(sketch, "E21.11.0.62", {"start": v(-9.48, -58) * mm, "mid": v(-8.6, -60.12) * mm, "end": v(-6.48, -61) * mm});
            skArc(sketch, "E21.15.0.62", {"start": v(-6.48, -55) * mm, "mid": v(-8.6, -55.88) * mm, "end": v(-9.48, -58) * mm});
            skArc(sketch, "E21.19.0.62", {"start": v(9.48, -58) * mm, "mid": v(8.6, -55.88) * mm, "end": v(6.48, -55) * mm});
            skArc(sketch, "E21.23.0.62", {"start": v(6.48, -61) * mm, "mid": v(8.6, -60.12) * mm, "end": v(9.48, -58) * mm});
            skLineSegment(sketch, "E21.0.0.63", {"start": v(-6.48, -46) * mm, "end": v(6.48, -46) * mm});
            skLineSegment(sketch, "E21.3.0.63", {"start": v(-6.48, -40) * mm, "end": v(6.48, -40) * mm});
            skPoint(sketch, "E21.6.0.63", {"position": v(9.48, -40) * mm});
            skPoint(sketch, "E21.7.0.63", {"position": v(-9.48, -46) * mm});
            skPoint(sketch, "E21.8.0.63", {"position": v(9.48, -46) * mm});
            skPoint(sketch, "E21.9.0.63", {"position": v(-9.48, -40) * mm});
            skPoint(sketch, "E21.10.0.63", {"position": v(0, -43) * mm});
            skArc(sketch, "E21.11.0.63", {"start": v(-9.48, -43) * mm, "mid": v(-8.6, -45.12) * mm, "end": v(-6.48, -46) * mm});
            skArc(sketch, "E21.15.0.63", {"start": v(-6.48, -40) * mm, "mid": v(-8.6, -40.88) * mm, "end": v(-9.48, -43) * mm});
            skArc(sketch, "E21.19.0.63", {"start": v(9.48, -43) * mm, "mid": v(8.6, -40.88) * mm, "end": v(6.48, -40) * mm});
            skArc(sketch, "E21.23.0.63", {"start": v(6.48, -46) * mm, "mid": v(8.6, -45.12) * mm, "end": v(9.48, -43) * mm});
            skLineSegment(sketch, "E21.0.0.64", {"start": v(-6.48, -31) * mm, "end": v(6.48, -31) * mm});
            skLineSegment(sketch, "E21.3.0.64", {"start": v(-6.48, -25) * mm, "end": v(6.48, -25) * mm});
            skPoint(sketch, "E21.6.0.64", {"position": v(9.48, -25) * mm});
            skPoint(sketch, "E21.7.0.64", {"position": v(-9.48, -31) * mm});
            skPoint(sketch, "E21.8.0.64", {"position": v(9.48, -31) * mm});
            skPoint(sketch, "E21.9.0.64", {"position": v(-9.48, -25) * mm});
            skPoint(sketch, "E21.10.0.64", {"position": v(0, -28) * mm});
            skArc(sketch, "E21.11.0.64", {"start": v(-9.48, -28) * mm, "mid": v(-8.6, -30.12) * mm, "end": v(-6.48, -31) * mm});
            skArc(sketch, "E21.15.0.64", {"start": v(-6.48, -25) * mm, "mid": v(-8.6, -25.88) * mm, "end": v(-9.48, -28) * mm});
            skArc(sketch, "E21.19.0.64", {"start": v(9.48, -28) * mm, "mid": v(8.6, -25.88) * mm, "end": v(6.48, -25) * mm});
            skArc(sketch, "E21.23.0.64", {"start": v(6.48, -31) * mm, "mid": v(8.6, -30.12) * mm, "end": v(9.48, -28) * mm});
            skLineSegment(sketch, "E22.0.0.65", {"start": v(-6.48, -16) * mm, "end": v(6.48, -16) * mm});
            skLineSegment(sketch, "E22.3.0.65", {"start": v(-6.48, -10) * mm, "end": v(6.48, -10) * mm});
            skPoint(sketch, "E22.6.0.65", {"position": v(9.48, -10) * mm});
            skPoint(sketch, "E22.7.0.65", {"position": v(-9.48, -16) * mm});
            skPoint(sketch, "E22.8.0.65", {"position": v(9.48, -16) * mm});
            skPoint(sketch, "E22.9.0.65", {"position": v(-9.48, -10) * mm});
            skPoint(sketch, "E22.10.0.65", {"position": v(0, -13) * mm});
            skArc(sketch, "E22.11.0.65", {"start": v(-9.48, -13) * mm, "mid": v(-8.6, -15.12) * mm, "end": v(-6.48, -16) * mm});
            skArc(sketch, "E22.15.0.65", {"start": v(-6.48, -10) * mm, "mid": v(-8.6, -10.88) * mm, "end": v(-9.48, -13) * mm});
            skArc(sketch, "E22.19.0.65", {"start": v(9.48, -13) * mm, "mid": v(8.6, -10.88) * mm, "end": v(6.48, -10) * mm});
            skArc(sketch, "E22.23.0.65", {"start": v(6.48, -16) * mm, "mid": v(8.6, -15.12) * mm, "end": v(9.48, -13) * mm});
            skSolve(sketch);
        }
        {
            var Q0;
            Q0 = qSketchRegion(id + "F2", true);
            extrude(context, id + "F3", {"entities" : qUnion([Q0]), "operationType" : NewBodyOperationType.REMOVE, "endBound" : BoundingType.THROUGH_ALL, "oppositeDirection" : true, "depth" : 25 * mm});
        }
    });
